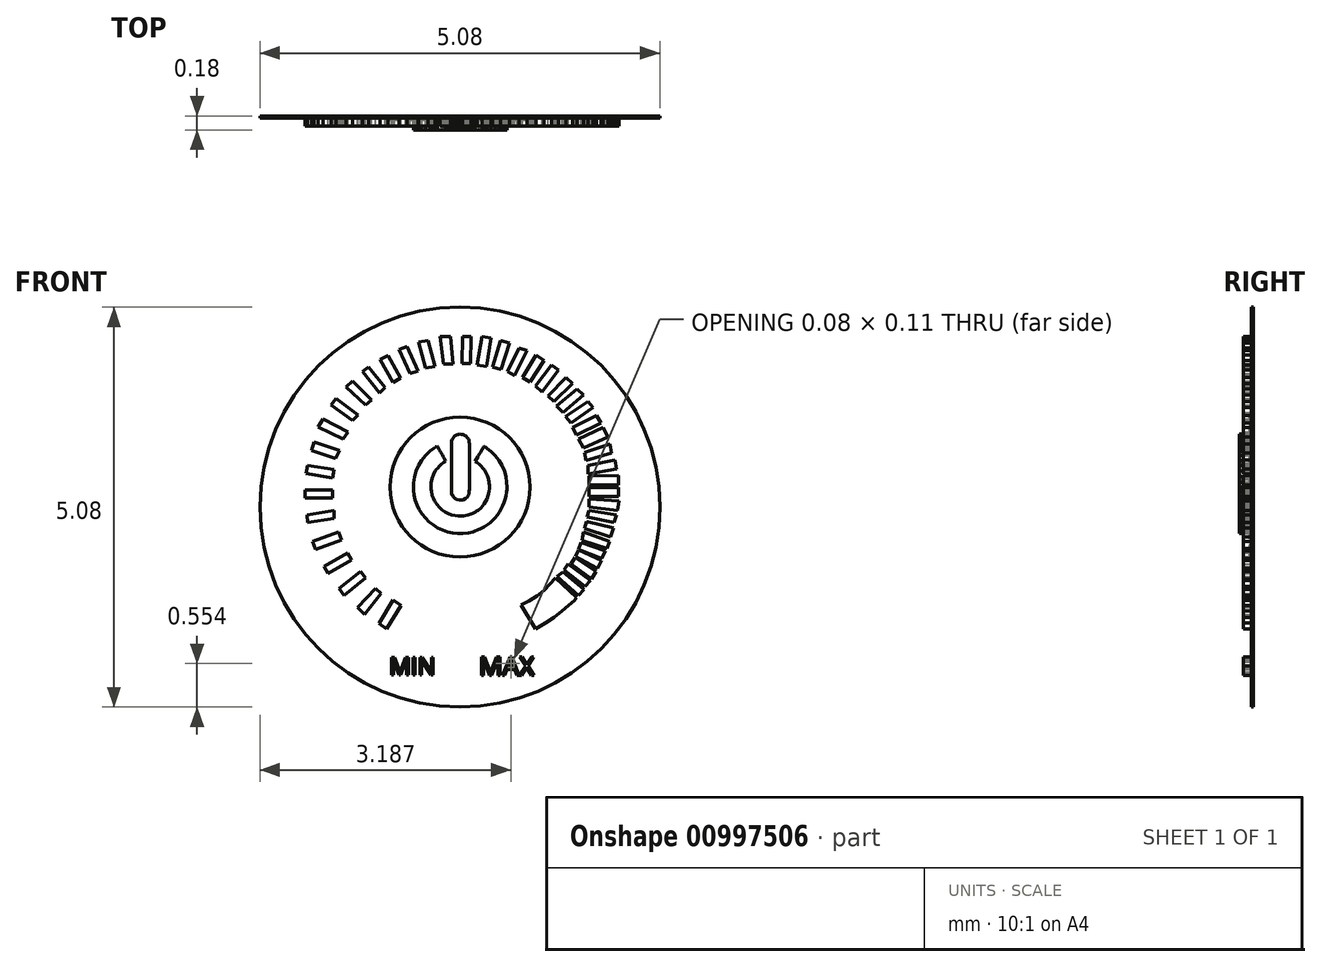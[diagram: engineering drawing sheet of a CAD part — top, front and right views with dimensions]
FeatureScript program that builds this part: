
annotation { "Feature Type Name" : "Feature", "Feature Type Description" : "" }
export const myFeature = defineFeature(function(context is Context, id is Id, definition is map)
    precondition{}
    {
        {
            var Q0;
            Q0=qCreatedBy(makeId("Front.planeOp"),FACE);
            var sketch = newSketch(context, id + "F0", { "sketchPlane" : qUnion([Q0])});
            skCircle(sketch, "E0", {"center": v(0, 0) * mm, "radius": 2.54 * mm});
            skSolve(sketch);
        }
        {
            var Q0;
            Q0 = qSketchRegion(id + "F0", true);
            extrude(context, id + "F1", {"entities" : qUnion([Q0]), "depth" : 0.03 * mm, "offsetDistance" : 25.4 * mm});
        }
        {
            var Q0;
            Q0=qCreatedBy(makeId("Front.planeOp"),FACE);
            var sketch = newSketch(context, id + "F2", { "sketchPlane" : qUnion([Q0])});
            skLineSegment(sketch, "E1", {"start": v(-0.85, -1.18) * mm, "end": v(-1.03, -1.48) * mm});
            skLineSegment(sketch, "E2", {"start": v(-1.03, -1.48) * mm, "end": v(-0.93, -1.55) * mm});
            skLineSegment(sketch, "E3", {"start": v(-0.93, -1.55) * mm, "end": v(-0.75, -1.25) * mm});
            skLineSegment(sketch, "E4", {"start": v(-0.75, -1.25) * mm, "end": v(-0.85, -1.18) * mm});
            skLineSegment(sketch, "E5", {"start": v(-1.3, -1.28) * mm, "end": v(-1.21, -1.36) * mm});
            skLineSegment(sketch, "E6", {"start": v(-1.21, -1.36) * mm, "end": v(-1, -1.1) * mm});
            skLineSegment(sketch, "E7", {"start": v(-1, -1.1) * mm, "end": v(-1.07, -1.03) * mm});
            skLineSegment(sketch, "E8", {"start": v(-1.07, -1.03) * mm, "end": v(-1.3, -1.28) * mm});
            skLineSegment(sketch, "E9", {"start": v(-1.54, -1.03) * mm, "end": v(-1.47, -1.12) * mm});
            skLineSegment(sketch, "E10", {"start": v(-1.47, -1.12) * mm, "end": v(-1.2, -0.9) * mm});
            skLineSegment(sketch, "E11", {"start": v(-1.2, -0.9) * mm, "end": v(-1.27, -0.82) * mm});
            skLineSegment(sketch, "E12", {"start": v(-1.27, -0.82) * mm, "end": v(-1.54, -1.03) * mm});
            skLineSegment(sketch, "E13", {"start": v(-1.73, -0.75) * mm, "end": v(-1.67, -0.85) * mm});
            skLineSegment(sketch, "E14", {"start": v(-1.67, -0.85) * mm, "end": v(-1.38, -0.67) * mm});
            skLineSegment(sketch, "E15", {"start": v(-1.38, -0.67) * mm, "end": v(-1.43, -0.58) * mm});
            skLineSegment(sketch, "E16", {"start": v(-1.43, -0.58) * mm, "end": v(-1.73, -0.75) * mm});
            skLineSegment(sketch, "E17", {"start": v(-1.87, -0.43) * mm, "end": v(-1.83, -0.54) * mm});
            skLineSegment(sketch, "E18", {"start": v(-1.83, -0.54) * mm, "end": v(-1.5, -0.42) * mm});
            skLineSegment(sketch, "E19", {"start": v(-1.5, -0.42) * mm, "end": v(-1.54, -0.32) * mm});
            skLineSegment(sketch, "E20", {"start": v(-1.54, -0.32) * mm, "end": v(-1.87, -0.43) * mm});
            skLineSegment(sketch, "E21", {"start": v(-1.94, -0.1) * mm, "end": v(-1.94, -0.2) * mm});
            skLineSegment(sketch, "E22", {"start": v(-1.94, -0.2) * mm, "end": v(-1.6, -0.14) * mm});
            skLineSegment(sketch, "E23", {"start": v(-1.6, -0.14) * mm, "end": v(-1.6, -0.04) * mm});
            skLineSegment(sketch, "E24", {"start": v(-1.6, -0.04) * mm, "end": v(-1.94, -0.1) * mm});
            skLineSegment(sketch, "E25", {"start": v(-1.97, 0.22) * mm, "end": v(-1.97, 0.12) * mm});
            skLineSegment(sketch, "E26", {"start": v(-1.97, 0.12) * mm, "end": v(-1.62, 0.12) * mm});
            skLineSegment(sketch, "E27", {"start": v(-1.62, 0.12) * mm, "end": v(-1.62, 0.22) * mm});
            skLineSegment(sketch, "E28", {"start": v(-1.62, 0.22) * mm, "end": v(-1.97, 0.22) * mm});
            skLineSegment(sketch, "E29", {"start": v(-1.94, 0.53) * mm, "end": v(-1.96, 0.43) * mm});
            skLineSegment(sketch, "E30", {"start": v(-1.96, 0.43) * mm, "end": v(-1.62, 0.37) * mm});
            skLineSegment(sketch, "E31", {"start": v(-1.62, 0.37) * mm, "end": v(-1.6, 0.48) * mm});
            skLineSegment(sketch, "E32", {"start": v(-1.6, 0.48) * mm, "end": v(-1.94, 0.53) * mm});
            skLineSegment(sketch, "E33", {"start": v(-1.85, 0.82) * mm, "end": v(-1.89, 0.72) * mm});
            skLineSegment(sketch, "E34", {"start": v(-1.89, 0.72) * mm, "end": v(-1.58, 0.62) * mm});
            skLineSegment(sketch, "E35", {"start": v(-1.58, 0.62) * mm, "end": v(-1.53, 0.72) * mm});
            skLineSegment(sketch, "E36", {"start": v(-1.53, 0.72) * mm, "end": v(-1.85, 0.82) * mm});
            skLineSegment(sketch, "E37", {"start": v(-1.74, 1.12) * mm, "end": v(-1.8, 1.02) * mm});
            skLineSegment(sketch, "E38", {"start": v(-1.8, 1.02) * mm, "end": v(-1.48, 0.86) * mm});
            skLineSegment(sketch, "E39", {"start": v(-1.48, 0.86) * mm, "end": v(-1.42, 0.95) * mm});
            skLineSegment(sketch, "E40", {"start": v(-1.42, 0.95) * mm, "end": v(-1.74, 1.12) * mm});
            skLineSegment(sketch, "E41", {"start": v(-1.57, 1.38) * mm, "end": v(-1.64, 1.3) * mm});
            skLineSegment(sketch, "E42", {"start": v(-1.64, 1.3) * mm, "end": v(-1.36, 1.1) * mm});
            skLineSegment(sketch, "E43", {"start": v(-1.36, 1.1) * mm, "end": v(-1.3, 1.17) * mm});
            skLineSegment(sketch, "E44", {"start": v(-1.3, 1.17) * mm, "end": v(-1.57, 1.38) * mm});
            skLineSegment(sketch, "E45", {"start": v(-1.45, 1.53) * mm, "end": v(-1.2, 1.3) * mm});
            skLineSegment(sketch, "E46", {"start": v(-1.2, 1.3) * mm, "end": v(-1.12, 1.36) * mm});
            skLineSegment(sketch, "E47", {"start": v(-1.12, 1.36) * mm, "end": v(-1.36, 1.6) * mm});
            skLineSegment(sketch, "E48", {"start": v(-1.36, 1.6) * mm, "end": v(-1.45, 1.53) * mm});
            skLineSegment(sketch, "E49", {"start": v(-1.24, 1.72) * mm, "end": v(-1.16, 1.78) * mm});
            skLineSegment(sketch, "E50", {"start": v(-1.16, 1.78) * mm, "end": v(-0.95, 1.52) * mm});
            skLineSegment(sketch, "E51", {"start": v(-0.95, 1.52) * mm, "end": v(-1.02, 1.45) * mm});
            skLineSegment(sketch, "E52", {"start": v(-1.02, 1.45) * mm, "end": v(-1.24, 1.72) * mm});
            skLineSegment(sketch, "E53", {"start": v(-1.01, 1.88) * mm, "end": v(-0.85, 1.58) * mm});
            skLineSegment(sketch, "E54", {"start": v(-0.85, 1.58) * mm, "end": v(-0.75, 1.64) * mm});
            skLineSegment(sketch, "E55", {"start": v(-0.75, 1.64) * mm, "end": v(-0.91, 1.93) * mm});
            skLineSegment(sketch, "E56", {"start": v(-0.91, 1.93) * mm, "end": v(-1.01, 1.88) * mm});
            skLineSegment(sketch, "E57", {"start": v(-0.77, 2) * mm, "end": v(-0.63, 1.7) * mm});
            skLineSegment(sketch, "E58", {"start": v(-0.63, 1.7) * mm, "end": v(-0.53, 1.73) * mm});
            skLineSegment(sketch, "E59", {"start": v(-0.53, 1.73) * mm, "end": v(-0.67, 2.04) * mm});
            skLineSegment(sketch, "E60", {"start": v(-0.67, 2.04) * mm, "end": v(-0.77, 2) * mm});
            skLineSegment(sketch, "E61", {"start": v(-0.53, 2.1) * mm, "end": v(-0.4, 2.12) * mm});
            skLineSegment(sketch, "E62", {"start": v(-0.4, 2.12) * mm, "end": v(-0.32, 1.79) * mm});
            skLineSegment(sketch, "E63", {"start": v(-0.32, 1.79) * mm, "end": v(-0.44, 1.77) * mm});
            skLineSegment(sketch, "E64", {"start": v(-0.44, 1.77) * mm, "end": v(-0.53, 2.1) * mm});
            skLineSegment(sketch, "E65", {"start": v(-0.25, 2.17) * mm, "end": v(-0.21, 1.82) * mm});
            skLineSegment(sketch, "E66", {"start": v(-0.21, 1.82) * mm, "end": v(-0.1, 1.82) * mm});
            skLineSegment(sketch, "E67", {"start": v(-0.1, 1.82) * mm, "end": v(-0.12, 2.17) * mm});
            skLineSegment(sketch, "E68", {"start": v(-0.12, 2.17) * mm, "end": v(-0.25, 2.17) * mm});
            skLineSegment(sketch, "E69", {"start": v(0.03, 2.17) * mm, "end": v(0.03, 1.83) * mm});
            skLineSegment(sketch, "E70", {"start": v(0.03, 1.83) * mm, "end": v(0.13, 1.82) * mm});
            skLineSegment(sketch, "E71", {"start": v(0.13, 1.82) * mm, "end": v(0.14, 2.17) * mm});
            skLineSegment(sketch, "E72", {"start": v(0.14, 2.17) * mm, "end": v(0.03, 2.17) * mm});
            skLineSegment(sketch, "E73", {"start": v(0.22, 1.8) * mm, "end": v(0.33, 1.79) * mm});
            skLineSegment(sketch, "E74", {"start": v(0.33, 1.79) * mm, "end": v(0.4, 2.15) * mm});
            skLineSegment(sketch, "E75", {"start": v(0.4, 2.15) * mm, "end": v(0.28, 2.16) * mm});
            skLineSegment(sketch, "E76", {"start": v(0.28, 2.16) * mm, "end": v(0.22, 1.8) * mm});
            skLineSegment(sketch, "E77", {"start": v(0.42, 1.78) * mm, "end": v(0.52, 1.75) * mm});
            skLineSegment(sketch, "E78", {"start": v(0.52, 1.75) * mm, "end": v(0.63, 2.08) * mm});
            skLineSegment(sketch, "E79", {"start": v(0.63, 2.08) * mm, "end": v(0.52, 2.12) * mm});
            skLineSegment(sketch, "E80", {"start": v(0.52, 2.12) * mm, "end": v(0.42, 1.78) * mm});
            skLineSegment(sketch, "E81", {"start": v(0.6, 1.72) * mm, "end": v(0.7, 1.67) * mm});
            skLineSegment(sketch, "E82", {"start": v(0.7, 1.67) * mm, "end": v(0.85, 1.99) * mm});
            skLineSegment(sketch, "E83", {"start": v(0.85, 1.99) * mm, "end": v(0.75, 2.02) * mm});
            skLineSegment(sketch, "E84", {"start": v(0.75, 2.02) * mm, "end": v(0.6, 1.72) * mm});
            skLineSegment(sketch, "E85", {"start": v(0.8, 1.65) * mm, "end": v(0.89, 1.59) * mm});
            skLineSegment(sketch, "E86", {"start": v(0.89, 1.59) * mm, "end": v(1.07, 1.86) * mm});
            skLineSegment(sketch, "E87", {"start": v(1.07, 1.86) * mm, "end": v(0.96, 1.93) * mm});
            skLineSegment(sketch, "E88", {"start": v(0.96, 1.93) * mm, "end": v(0.8, 1.65) * mm});
            skLineSegment(sketch, "E89", {"start": v(0.96, 1.54) * mm, "end": v(1.04, 1.46) * mm});
            skLineSegment(sketch, "E90", {"start": v(1.04, 1.46) * mm, "end": v(1.25, 1.74) * mm});
            skLineSegment(sketch, "E91", {"start": v(1.25, 1.74) * mm, "end": v(1.16, 1.8) * mm});
            skLineSegment(sketch, "E92", {"start": v(1.16, 1.8) * mm, "end": v(0.96, 1.54) * mm});
            skLineSegment(sketch, "E93", {"start": v(1.12, 1.41) * mm, "end": v(1.2, 1.34) * mm});
            skLineSegment(sketch, "E94", {"start": v(1.2, 1.34) * mm, "end": v(1.43, 1.57) * mm});
            skLineSegment(sketch, "E95", {"start": v(1.43, 1.57) * mm, "end": v(1.35, 1.65) * mm});
            skLineSegment(sketch, "E96", {"start": v(1.35, 1.65) * mm, "end": v(1.12, 1.41) * mm});
            skLineSegment(sketch, "E97", {"start": v(1.22, 1.29) * mm, "end": v(1.3, 1.2) * mm});
            skLineSegment(sketch, "E98", {"start": v(1.3, 1.2) * mm, "end": v(1.57, 1.42) * mm});
            skLineSegment(sketch, "E99", {"start": v(1.57, 1.42) * mm, "end": v(1.49, 1.5) * mm});
            skLineSegment(sketch, "E100", {"start": v(1.49, 1.5) * mm, "end": v(1.22, 1.29) * mm});
            skLineSegment(sketch, "E101", {"start": v(1.34, 1.15) * mm, "end": v(1.41, 1.07) * mm});
            skLineSegment(sketch, "E102", {"start": v(1.41, 1.07) * mm, "end": v(1.69, 1.26) * mm});
            skLineSegment(sketch, "E103", {"start": v(1.69, 1.26) * mm, "end": v(1.63, 1.34) * mm});
            skLineSegment(sketch, "E104", {"start": v(1.63, 1.34) * mm, "end": v(1.34, 1.15) * mm});
            skLineSegment(sketch, "E105", {"start": v(1.43, 1) * mm, "end": v(1.48, 0.92) * mm});
            skLineSegment(sketch, "E106", {"start": v(1.48, 0.92) * mm, "end": v(1.8, 1.07) * mm});
            skLineSegment(sketch, "E107", {"start": v(1.8, 1.07) * mm, "end": v(1.74, 1.17) * mm});
            skLineSegment(sketch, "E108", {"start": v(1.74, 1.17) * mm, "end": v(1.43, 1) * mm});
            skLineSegment(sketch, "E109", {"start": v(1.5, 0.86) * mm, "end": v(1.57, 0.75) * mm});
            skLineSegment(sketch, "E110", {"start": v(1.57, 0.75) * mm, "end": v(1.88, 0.9) * mm});
            skLineSegment(sketch, "E111", {"start": v(1.88, 0.9) * mm, "end": v(1.82, 1) * mm});
            skLineSegment(sketch, "E112", {"start": v(1.82, 1) * mm, "end": v(1.5, 0.86) * mm});
            skLineSegment(sketch, "E113", {"start": v(1.58, 0.7) * mm, "end": v(1.6, 0.6) * mm});
            skLineSegment(sketch, "E114", {"start": v(1.6, 0.6) * mm, "end": v(1.93, 0.69) * mm});
            skLineSegment(sketch, "E115", {"start": v(1.93, 0.69) * mm, "end": v(1.9, 0.8) * mm});
            skLineSegment(sketch, "E116", {"start": v(1.9, 0.8) * mm, "end": v(1.58, 0.7) * mm});
            skLineSegment(sketch, "E117", {"start": v(1.62, 0.53) * mm, "end": v(1.62, 0.42) * mm});
            skLineSegment(sketch, "E118", {"start": v(1.62, 0.42) * mm, "end": v(1.99, 0.49) * mm});
            skLineSegment(sketch, "E119", {"start": v(1.99, 0.49) * mm, "end": v(1.97, 0.6) * mm});
            skLineSegment(sketch, "E120", {"start": v(1.97, 0.6) * mm, "end": v(1.62, 0.53) * mm});
            skLineSegment(sketch, "E121", {"start": v(1.64, 0.4) * mm, "end": v(1.64, 0.28) * mm});
            skLineSegment(sketch, "E122", {"start": v(1.64, 0.28) * mm, "end": v(2.02, 0.28) * mm});
            skLineSegment(sketch, "E123", {"start": v(2.02, 0.28) * mm, "end": v(2.02, 0.4) * mm});
            skLineSegment(sketch, "E124", {"start": v(2.02, 0.4) * mm, "end": v(1.64, 0.4) * mm});
            skLineSegment(sketch, "E125", {"start": v(1.64, 0.25) * mm, "end": v(1.64, 0.14) * mm});
            skLineSegment(sketch, "E126", {"start": v(1.64, 0.14) * mm, "end": v(2.02, 0.14) * mm});
            skLineSegment(sketch, "E127", {"start": v(2.02, 0.14) * mm, "end": v(2.02, 0.25) * mm});
            skLineSegment(sketch, "E128", {"start": v(2.02, 0.25) * mm, "end": v(1.64, 0.25) * mm});
            skLineSegment(sketch, "E129", {"start": v(1.64, 0.1) * mm, "end": v(1.64, 0) * mm});
            skLineSegment(sketch, "E130", {"start": v(1.64, 0) * mm, "end": v(2, -0.04) * mm});
            skLineSegment(sketch, "E131", {"start": v(2, -0.04) * mm, "end": v(2.02, 0.08) * mm});
            skLineSegment(sketch, "E132", {"start": v(2.02, 0.08) * mm, "end": v(1.64, 0.1) * mm});
            skLineSegment(sketch, "E133", {"start": v(1.64, -0.04) * mm, "end": v(1.61, -0.12) * mm});
            skLineSegment(sketch, "E134", {"start": v(1.61, -0.12) * mm, "end": v(1.96, -0.2) * mm});
            skLineSegment(sketch, "E135", {"start": v(1.96, -0.2) * mm, "end": v(1.99, -0.1) * mm});
            skLineSegment(sketch, "E136", {"start": v(1.99, -0.1) * mm, "end": v(1.64, -0.04) * mm});
            skLineSegment(sketch, "E137", {"start": v(1.6, -0.19) * mm, "end": v(1.58, -0.27) * mm});
            skLineSegment(sketch, "E138", {"start": v(1.58, -0.27) * mm, "end": v(1.91, -0.38) * mm});
            skLineSegment(sketch, "E139", {"start": v(1.91, -0.38) * mm, "end": v(1.95, -0.27) * mm});
            skLineSegment(sketch, "E140", {"start": v(1.95, -0.27) * mm, "end": v(1.6, -0.19) * mm});
            skLineSegment(sketch, "E141", {"start": v(0.78, -1.24) * mm, "end": v(0.96, -1.55) * mm});
            skLineSegment(sketch, "E142", {"start": v(0.96, -1.55) * mm, "end": v(1.09, -1.47) * mm});
            skLineSegment(sketch, "E143", {"start": v(1.09, -1.47) * mm, "end": v(1.2, -1.4) * mm});
            skLineSegment(sketch, "E144", {"start": v(1.2, -1.4) * mm, "end": v(1.3, -1.32) * mm});
            skLineSegment(sketch, "E145", {"start": v(1.3, -1.32) * mm, "end": v(1.38, -1.25) * mm});
            skLineSegment(sketch, "E146", {"start": v(1.38, -1.25) * mm, "end": v(1.46, -1.19) * mm});
            skLineSegment(sketch, "E147", {"start": v(1.46, -1.19) * mm, "end": v(1.48, -1.15) * mm});
            skLineSegment(sketch, "E148", {"start": v(1.48, -1.15) * mm, "end": v(1.22, -0.9) * mm});
            skLineSegment(sketch, "E149", {"start": v(1.22, -0.9) * mm, "end": v(1.14, -0.98) * mm});
            skLineSegment(sketch, "E150", {"start": v(1.14, -0.98) * mm, "end": v(1.07, -1.06) * mm});
            skLineSegment(sketch, "E151", {"start": v(1.07, -1.06) * mm, "end": v(0.98, -1.13) * mm});
            skLineSegment(sketch, "E152", {"start": v(0.98, -1.13) * mm, "end": v(0.88, -1.2) * mm});
            skLineSegment(sketch, "E153", {"start": v(0.88, -1.2) * mm, "end": v(0.78, -1.24) * mm});
            skLineSegment(sketch, "E154", {"start": v(1.5, -1.12) * mm, "end": v(1.23, -0.88) * mm});
            skLineSegment(sketch, "E155", {"start": v(1.23, -0.88) * mm, "end": v(1.3, -0.82) * mm});
            skLineSegment(sketch, "E156", {"start": v(1.3, -0.82) * mm, "end": v(1.57, -1.05) * mm});
            skLineSegment(sketch, "E157", {"start": v(1.57, -1.05) * mm, "end": v(1.5, -1.12) * mm});
            skLineSegment(sketch, "E158", {"start": v(1.59, -1) * mm, "end": v(1.66, -0.93) * mm});
            skLineSegment(sketch, "E159", {"start": v(1.66, -0.93) * mm, "end": v(1.37, -0.72) * mm});
            skLineSegment(sketch, "E160", {"start": v(1.37, -0.72) * mm, "end": v(1.32, -0.8) * mm});
            skLineSegment(sketch, "E161", {"start": v(1.32, -0.8) * mm, "end": v(1.59, -1) * mm});
            skLineSegment(sketch, "E162", {"start": v(1.57, -0.32) * mm, "end": v(1.55, -0.43) * mm});
            skLineSegment(sketch, "E163", {"start": v(1.55, -0.43) * mm, "end": v(1.87, -0.53) * mm});
            skLineSegment(sketch, "E164", {"start": v(1.87, -0.53) * mm, "end": v(1.9, -0.43) * mm});
            skLineSegment(sketch, "E165", {"start": v(1.9, -0.43) * mm, "end": v(1.57, -0.32) * mm});
            skLineSegment(sketch, "E166", {"start": v(1.8, -0.65) * mm, "end": v(1.85, -0.56) * mm});
            skLineSegment(sketch, "E167", {"start": v(1.85, -0.56) * mm, "end": v(1.54, -0.45) * mm});
            skLineSegment(sketch, "E168", {"start": v(1.54, -0.45) * mm, "end": v(1.5, -0.54) * mm});
            skLineSegment(sketch, "E169", {"start": v(1.5, -0.54) * mm, "end": v(1.8, -0.65) * mm});
            skLineSegment(sketch, "E170", {"start": v(1.5, -0.55) * mm, "end": v(1.47, -0.62) * mm});
            skLineSegment(sketch, "E171", {"start": v(1.47, -0.62) * mm, "end": v(1.75, -0.78) * mm});
            skLineSegment(sketch, "E172", {"start": v(1.75, -0.78) * mm, "end": v(1.8, -0.68) * mm});
            skLineSegment(sketch, "E173", {"start": v(1.8, -0.68) * mm, "end": v(1.5, -0.55) * mm});
            skLineSegment(sketch, "E174", {"start": v(1.67, -0.91) * mm, "end": v(1.73, -0.82) * mm});
            skLineSegment(sketch, "E175", {"start": v(1.73, -0.82) * mm, "end": v(1.46, -0.64) * mm});
            skLineSegment(sketch, "E176", {"start": v(1.46, -0.64) * mm, "end": v(1.41, -0.72) * mm});
            skLineSegment(sketch, "E177", {"start": v(1.41, -0.72) * mm, "end": v(1.67, -0.91) * mm});
            skText(sketch, "E178", { "text": "MIN", "fontName": "OpenSans-Regular.ttf"});
            skText(sketch, "E179", { "text": "MAX", "fontName": "OpenSans-Regular.ttf"});
            const initialGuessF2  = {"E178": [-0.0009, -0.00213, 1, 0, 0.00022], "E179": [0.00024, -0.00214, 1, 0, 0.00024]};
            skSetInitialGuess(sketch, initialGuessF2);
            skSolve(sketch);
        }
        {
            var Q0;
            Q0 = qSketchRegion(id + "F2", true);
            extrude(context, id + "F3", {"entities" : qUnion([Q0]), "depth" : 0.13 * mm, "offsetDistance" : 25.4 * mm});
        }
        {
            var Q0;
            Q0=makeQuery(id+"F1.opExtrude","CAP_FACE",FACE,{"disambiguationData":[OSD([sQuery(id+"F0.wireOp",EDGE,"E0")])],"isStart":false});
            var sketch = newSketch(context, id + "F4", { "sketchPlane" : qUnion([Q0])});
            skCircle(sketch, "E180", {"center": v(0, 0.25) * mm, "radius": 0.89 * mm});
            skSolve(sketch);
        }
        {
            var Q0;
            Q0=makeQuery(id+"F4.imprint","IMPRINT",FACE,{"disambiguationData":[TD([[makeQuery(id+"F4.imprint","IMPRINT",EDGE,{"derivedFrom":sQuery(id+"F4.wireOp",EDGE,"E180")}),1.0]])]});
            extrude(context, id + "F5", {"entities" : qUnion([Q0]), "depth" : 0.03 * mm, "offsetDistance" : 25.4 * mm});
        }
        {
            var Q0;
            Q0=makeQuery(id+"F5.opExtrude","CAP_FACE",FACE,{"disambiguationData":[OSD([sQuery(id+"F4.wireOp",EDGE,"E180")])],"isStart":false});
            var sketch = newSketch(context, id + "F6", { "sketchPlane" : qUnion([Q0])});
            skPoint(sketch, "E181", {"position": v(0, 0.34) * mm});
            skLineSegment(sketch, "E182", {"start": v(-0.02, 0.92) * mm, "end": v(-0.03, 0.92) * mm});
            skLineSegment(sketch, "E183", {"start": v(-0.03, 0.92) * mm, "end": v(-0.05, 0.92) * mm});
            skLineSegment(sketch, "E184", {"start": v(-0.05, 0.92) * mm, "end": v(-0.07, 0.9) * mm});
            skLineSegment(sketch, "E185", {"start": v(-0.07, 0.9) * mm, "end": v(-0.08, 0.88) * mm});
            skLineSegment(sketch, "E186", {"start": v(-0.08, 0.88) * mm, "end": v(-0.1, 0.86) * mm});
            skLineSegment(sketch, "E187", {"start": v(-0.1, 0.86) * mm, "end": v(-0.1, 0.86) * mm});
            skLineSegment(sketch, "E188", {"start": v(-0.1, 0.86) * mm, "end": v(-0.1, 0.84) * mm});
            skLineSegment(sketch, "E189", {"start": v(-0.1, 0.84) * mm, "end": v(-0.1, 0.18) * mm});
            skLineSegment(sketch, "E190", {"start": v(-0.1, 0.18) * mm, "end": v(-0.1, 0.16) * mm});
            skLineSegment(sketch, "E191", {"start": v(-0.1, 0.16) * mm, "end": v(-0.1, 0.15) * mm});
            skLineSegment(sketch, "E192", {"start": v(-0.1, 0.15) * mm, "end": v(-0.09, 0.14) * mm});
            skLineSegment(sketch, "E193", {"start": v(-0.09, 0.14) * mm, "end": v(-0.08, 0.12) * mm});
            skLineSegment(sketch, "E194", {"start": v(-0.08, 0.12) * mm, "end": v(-0.06, 0.11) * mm});
            skLineSegment(sketch, "E195", {"start": v(-0.06, 0.11) * mm, "end": v(-0.05, 0.1) * mm});
            skLineSegment(sketch, "E196", {"start": v(-0.05, 0.1) * mm, "end": v(-0.05, 0.1) * mm});
            skLineSegment(sketch, "E197", {"start": v(-0.05, 0.1) * mm, "end": v(-0.04, 0.1) * mm});
            skLineSegment(sketch, "E198", {"start": v(-0.04, 0.1) * mm, "end": v(0, 0.09) * mm});
            skLineSegment(sketch, "E199", {"start": v(0, 0.09) * mm, "end": v(0.03, 0.09) * mm});
            skLineSegment(sketch, "E200", {"start": v(0.03, 0.09) * mm, "end": v(0.03, 0.1) * mm});
            skLineSegment(sketch, "E201", {"start": v(0.03, 0.1) * mm, "end": v(0.04, 0.1) * mm});
            skLineSegment(sketch, "E202", {"start": v(0.04, 0.1) * mm, "end": v(0.07, 0.1) * mm});
            skLineSegment(sketch, "E203", {"start": v(0.07, 0.1) * mm, "end": v(0.1, 0.13) * mm});
            skLineSegment(sketch, "E204", {"start": v(0.1, 0.13) * mm, "end": v(0.1, 0.14) * mm});
            skLineSegment(sketch, "E205", {"start": v(0.1, 0.14) * mm, "end": v(0.1, 0.14) * mm});
            skLineSegment(sketch, "E206", {"start": v(0.1, 0.14) * mm, "end": v(0.1, 0.15) * mm});
            skLineSegment(sketch, "E207", {"start": v(0.1, 0.15) * mm, "end": v(0.1, 0.15) * mm});
            skLineSegment(sketch, "E208", {"start": v(0.1, 0.15) * mm, "end": v(0.11, 0.16) * mm});
            skLineSegment(sketch, "E209", {"start": v(0.11, 0.16) * mm, "end": v(0.11, 0.17) * mm});
            skLineSegment(sketch, "E210", {"start": v(0.11, 0.17) * mm, "end": v(0.12, 0.18) * mm});
            skLineSegment(sketch, "E211", {"start": v(0.12, 0.18) * mm, "end": v(0.12, 0.19) * mm});
            skLineSegment(sketch, "E212", {"start": v(0.12, 0.19) * mm, "end": v(0.12, 0.2) * mm});
            skLineSegment(sketch, "E213", {"start": v(0.12, 0.2) * mm, "end": v(0.12, 0.22) * mm});
            skLineSegment(sketch, "E214", {"start": v(0.12, 0.22) * mm, "end": v(0.12, 0.24) * mm});
            skLineSegment(sketch, "E215", {"start": v(0.12, 0.24) * mm, "end": v(0.12, 0.27) * mm});
            skLineSegment(sketch, "E216", {"start": v(0.12, 0.27) * mm, "end": v(0.12, 0.3) * mm});
            skLineSegment(sketch, "E217", {"start": v(0.12, 0.3) * mm, "end": v(0.12, 0.35) * mm});
            skLineSegment(sketch, "E218", {"start": v(0.12, 0.35) * mm, "end": v(0.12, 0.4) * mm});
            skLineSegment(sketch, "E219", {"start": v(0.12, 0.4) * mm, "end": v(0.12, 0.45) * mm});
            skLineSegment(sketch, "E220", {"start": v(0.12, 0.45) * mm, "end": v(0.12, 0.5) * mm});
            skLineSegment(sketch, "E221", {"start": v(0.12, 0.5) * mm, "end": v(0.12, 0.5) * mm});
            skLineSegment(sketch, "E222", {"start": v(0.12, 0.5) * mm, "end": v(0.12, 0.53) * mm});
            skLineSegment(sketch, "E223", {"start": v(0.12, 0.53) * mm, "end": v(0.12, 0.6) * mm});
            skLineSegment(sketch, "E224", {"start": v(0.12, 0.6) * mm, "end": v(0.12, 0.68) * mm});
            skLineSegment(sketch, "E225", {"start": v(0.12, 0.68) * mm, "end": v(0.12, 0.73) * mm});
            skLineSegment(sketch, "E226", {"start": v(0.12, 0.73) * mm, "end": v(0.12, 0.77) * mm});
            skLineSegment(sketch, "E227", {"start": v(0.12, 0.77) * mm, "end": v(0.12, 0.8) * mm});
            skLineSegment(sketch, "E228", {"start": v(0.12, 0.8) * mm, "end": v(0.12, 0.82) * mm});
            skLineSegment(sketch, "E229", {"start": v(0.12, 0.82) * mm, "end": v(0.12, 0.84) * mm});
            skLineSegment(sketch, "E230", {"start": v(0.12, 0.84) * mm, "end": v(0.12, 0.84) * mm});
            skLineSegment(sketch, "E231", {"start": v(0.12, 0.84) * mm, "end": v(0.11, 0.84) * mm});
            skLineSegment(sketch, "E232", {"start": v(0.11, 0.84) * mm, "end": v(0.11, 0.85) * mm});
            skLineSegment(sketch, "E233", {"start": v(0.11, 0.85) * mm, "end": v(0.1, 0.87) * mm});
            skLineSegment(sketch, "E234", {"start": v(0.1, 0.87) * mm, "end": v(0.1, 0.89) * mm});
            skLineSegment(sketch, "E235", {"start": v(0.1, 0.89) * mm, "end": v(0.08, 0.9) * mm});
            skLineSegment(sketch, "E236", {"start": v(0.08, 0.9) * mm, "end": v(0.06, 0.91) * mm});
            skLineSegment(sketch, "E237", {"start": v(0.06, 0.91) * mm, "end": v(0.06, 0.92) * mm});
            skLineSegment(sketch, "E238", {"start": v(0.06, 0.92) * mm, "end": v(0.05, 0.92) * mm});
            skLineSegment(sketch, "E239", {"start": v(0.05, 0.92) * mm, "end": v(0.04, 0.92) * mm});
            skLineSegment(sketch, "E240", {"start": v(0.04, 0.92) * mm, "end": v(0.02, 0.93) * mm});
            skLineSegment(sketch, "E241", {"start": v(0.02, 0.93) * mm, "end": v(0, 0.93) * mm});
            skLineSegment(sketch, "E242", {"start": v(0, 0.93) * mm, "end": v(-0.02, 0.93) * mm});
            skLineSegment(sketch, "E243", {"start": v(-0.02, 0.93) * mm, "end": v(-0.02, 0.92) * mm});
            skLineSegment(sketch, "E244", {"start": v(-0.32, 0.76) * mm, "end": v(-0.33, 0.75) * mm});
            skLineSegment(sketch, "E245", {"start": v(-0.33, 0.75) * mm, "end": v(-0.38, 0.7) * mm});
            skLineSegment(sketch, "E246", {"start": v(-0.38, 0.7) * mm, "end": v(-0.44, 0.65) * mm});
            skLineSegment(sketch, "E247", {"start": v(-0.44, 0.65) * mm, "end": v(-0.49, 0.6) * mm});
            skLineSegment(sketch, "E248", {"start": v(-0.49, 0.6) * mm, "end": v(-0.53, 0.53) * mm});
            skLineSegment(sketch, "E249", {"start": v(-0.53, 0.53) * mm, "end": v(-0.56, 0.46) * mm});
            skLineSegment(sketch, "E250", {"start": v(-0.56, 0.46) * mm, "end": v(-0.58, 0.38) * mm});
            skLineSegment(sketch, "E251", {"start": v(-0.58, 0.38) * mm, "end": v(-0.59, 0.3) * mm});
            skLineSegment(sketch, "E252", {"start": v(-0.59, 0.3) * mm, "end": v(-0.6, 0.25) * mm});
            skLineSegment(sketch, "E253", {"start": v(-0.6, 0.25) * mm, "end": v(-0.6, 0.23) * mm});
            skLineSegment(sketch, "E254", {"start": v(-0.6, 0.23) * mm, "end": v(-0.59, 0.21) * mm});
            skLineSegment(sketch, "E255", {"start": v(-0.59, 0.21) * mm, "end": v(-0.58, 0.16) * mm});
            skLineSegment(sketch, "E256", {"start": v(-0.58, 0.16) * mm, "end": v(-0.57, 0.09) * mm});
            skLineSegment(sketch, "E257", {"start": v(-0.57, 0.09) * mm, "end": v(-0.54, 0.02) * mm});
            skLineSegment(sketch, "E258", {"start": v(-0.54, 0.02) * mm, "end": v(-0.51, -0.04) * mm});
            skLineSegment(sketch, "E259", {"start": v(-0.51, -0.04) * mm, "end": v(-0.48, -0.1) * mm});
            skLineSegment(sketch, "E260", {"start": v(-0.48, -0.1) * mm, "end": v(-0.44, -0.15) * mm});
            skLineSegment(sketch, "E261", {"start": v(-0.44, -0.15) * mm, "end": v(-0.39, -0.2) * mm});
            skLineSegment(sketch, "E262", {"start": v(-0.39, -0.2) * mm, "end": v(-0.34, -0.24) * mm});
            skLineSegment(sketch, "E263", {"start": v(-0.34, -0.24) * mm, "end": v(-0.28, -0.27) * mm});
            skLineSegment(sketch, "E264", {"start": v(-0.28, -0.27) * mm, "end": v(-0.22, -0.3) * mm});
            skLineSegment(sketch, "E265", {"start": v(-0.22, -0.3) * mm, "end": v(-0.16, -0.32) * mm});
            skLineSegment(sketch, "E266", {"start": v(-0.16, -0.32) * mm, "end": v(-0.1, -0.34) * mm});
            skLineSegment(sketch, "E267", {"start": v(-0.1, -0.34) * mm, "end": v(-0.02, -0.34) * mm});
            skLineSegment(sketch, "E268", {"start": v(-0.02, -0.34) * mm, "end": v(0.05, -0.34) * mm});
            skLineSegment(sketch, "E269", {"start": v(0.05, -0.34) * mm, "end": v(0.12, -0.33) * mm});
            skLineSegment(sketch, "E270", {"start": v(0.12, -0.33) * mm, "end": v(0.17, -0.32) * mm});
            skLineSegment(sketch, "E271", {"start": v(0.17, -0.32) * mm, "end": v(0.19, -0.32) * mm});
            skLineSegment(sketch, "E272", {"start": v(0.19, -0.32) * mm, "end": v(0.2, -0.31) * mm});
            skLineSegment(sketch, "E273", {"start": v(0.2, -0.31) * mm, "end": v(0.23, -0.3) * mm});
            skLineSegment(sketch, "E274", {"start": v(0.23, -0.3) * mm, "end": v(0.27, -0.28) * mm});
            skLineSegment(sketch, "E275", {"start": v(0.27, -0.28) * mm, "end": v(0.31, -0.26) * mm});
            skLineSegment(sketch, "E276", {"start": v(0.31, -0.26) * mm, "end": v(0.35, -0.23) * mm});
            skLineSegment(sketch, "E277", {"start": v(0.35, -0.23) * mm, "end": v(0.39, -0.2) * mm});
            skLineSegment(sketch, "E278", {"start": v(0.39, -0.2) * mm, "end": v(0.42, -0.18) * mm});
            skLineSegment(sketch, "E279", {"start": v(0.42, -0.18) * mm, "end": v(0.45, -0.14) * mm});
            skLineSegment(sketch, "E280", {"start": v(0.45, -0.14) * mm, "end": v(0.48, -0.1) * mm});
            skLineSegment(sketch, "E281", {"start": v(0.48, -0.1) * mm, "end": v(0.5, -0.07) * mm});
            skLineSegment(sketch, "E282", {"start": v(0.5, -0.07) * mm, "end": v(0.53, -0.03) * mm});
            skLineSegment(sketch, "E283", {"start": v(0.53, -0.03) * mm, "end": v(0.55, 0) * mm});
            skLineSegment(sketch, "E284", {"start": v(0.55, 0) * mm, "end": v(0.57, 0.05) * mm});
            skLineSegment(sketch, "E285", {"start": v(0.57, 0.05) * mm, "end": v(0.58, 0.1) * mm});
            skLineSegment(sketch, "E286", {"start": v(0.58, 0.1) * mm, "end": v(0.6, 0.14) * mm});
            skLineSegment(sketch, "E287", {"start": v(0.6, 0.14) * mm, "end": v(0.6, 0.18) * mm});
            skLineSegment(sketch, "E288", {"start": v(0.6, 0.18) * mm, "end": v(0.6, 0.22) * mm});
            skLineSegment(sketch, "E289", {"start": v(0.6, 0.22) * mm, "end": v(0.6, 0.23) * mm});
            skLineSegment(sketch, "E290", {"start": v(0.6, 0.23) * mm, "end": v(0.6, 0.25) * mm});
            skLineSegment(sketch, "E291", {"start": v(0.6, 0.25) * mm, "end": v(0.6, 0.3) * mm});
            skLineSegment(sketch, "E292", {"start": v(0.6, 0.3) * mm, "end": v(0.59, 0.38) * mm});
            skLineSegment(sketch, "E293", {"start": v(0.59, 0.38) * mm, "end": v(0.57, 0.46) * mm});
            skLineSegment(sketch, "E294", {"start": v(0.57, 0.46) * mm, "end": v(0.54, 0.53) * mm});
            skLineSegment(sketch, "E295", {"start": v(0.54, 0.53) * mm, "end": v(0.5, 0.6) * mm});
            skLineSegment(sketch, "E296", {"start": v(0.5, 0.6) * mm, "end": v(0.45, 0.65) * mm});
            skLineSegment(sketch, "E297", {"start": v(0.45, 0.65) * mm, "end": v(0.4, 0.7) * mm});
            skLineSegment(sketch, "E298", {"start": v(0.4, 0.7) * mm, "end": v(0.35, 0.74) * mm});
            skLineSegment(sketch, "E299", {"start": v(0.35, 0.74) * mm, "end": v(0.33, 0.76) * mm});
            skLineSegment(sketch, "E300", {"start": v(0.33, 0.76) * mm, "end": v(0.33, 0.76) * mm});
            skLineSegment(sketch, "E301", {"start": v(0.33, 0.76) * mm, "end": v(0.32, 0.76) * mm});
            skLineSegment(sketch, "E302", {"start": v(0.32, 0.76) * mm, "end": v(0.32, 0.77) * mm});
            skLineSegment(sketch, "E303", {"start": v(0.32, 0.77) * mm, "end": v(0.3, 0.77) * mm});
            skLineSegment(sketch, "E304", {"start": v(0.3, 0.77) * mm, "end": v(0.3, 0.77) * mm});
            skLineSegment(sketch, "E305", {"start": v(0.3, 0.77) * mm, "end": v(0.3, 0.76) * mm});
            skLineSegment(sketch, "E306", {"start": v(0.3, 0.76) * mm, "end": v(0.3, 0.75) * mm});
            skLineSegment(sketch, "E307", {"start": v(0.3, 0.75) * mm, "end": v(0.28, 0.74) * mm});
            skLineSegment(sketch, "E308", {"start": v(0.28, 0.74) * mm, "end": v(0.28, 0.74) * mm});
            skLineSegment(sketch, "E309", {"start": v(0.28, 0.74) * mm, "end": v(0.28, 0.73) * mm});
            skLineSegment(sketch, "E310", {"start": v(0.28, 0.73) * mm, "end": v(0.27, 0.72) * mm});
            skLineSegment(sketch, "E311", {"start": v(0.27, 0.72) * mm, "end": v(0.26, 0.7) * mm});
            skLineSegment(sketch, "E312", {"start": v(0.26, 0.7) * mm, "end": v(0.24, 0.67) * mm});
            skLineSegment(sketch, "E313", {"start": v(0.24, 0.67) * mm, "end": v(0.23, 0.65) * mm});
            skLineSegment(sketch, "E314", {"start": v(0.23, 0.65) * mm, "end": v(0.23, 0.64) * mm});
            skLineSegment(sketch, "E315", {"start": v(0.23, 0.64) * mm, "end": v(0.2, 0.58) * mm});
            skLineSegment(sketch, "E316", {"start": v(0.2, 0.58) * mm, "end": v(0.22, 0.56) * mm});
            skLineSegment(sketch, "E317", {"start": v(0.22, 0.56) * mm, "end": v(0.22, 0.55) * mm});
            skLineSegment(sketch, "E318", {"start": v(0.22, 0.55) * mm, "end": v(0.24, 0.54) * mm});
            skLineSegment(sketch, "E319", {"start": v(0.24, 0.54) * mm, "end": v(0.27, 0.51) * mm});
            skLineSegment(sketch, "E320", {"start": v(0.27, 0.51) * mm, "end": v(0.3, 0.49) * mm});
            skLineSegment(sketch, "E321", {"start": v(0.3, 0.49) * mm, "end": v(0.3, 0.47) * mm});
            skLineSegment(sketch, "E322", {"start": v(0.3, 0.47) * mm, "end": v(0.31, 0.46) * mm});
            skLineSegment(sketch, "E323", {"start": v(0.31, 0.46) * mm, "end": v(0.32, 0.45) * mm});
            skLineSegment(sketch, "E324", {"start": v(0.32, 0.45) * mm, "end": v(0.33, 0.43) * mm});
            skLineSegment(sketch, "E325", {"start": v(0.33, 0.43) * mm, "end": v(0.35, 0.39) * mm});
            skLineSegment(sketch, "E326", {"start": v(0.35, 0.39) * mm, "end": v(0.36, 0.35) * mm});
            skLineSegment(sketch, "E327", {"start": v(0.36, 0.35) * mm, "end": v(0.37, 0.32) * mm});
            skLineSegment(sketch, "E328", {"start": v(0.37, 0.32) * mm, "end": v(0.37, 0.31) * mm});
            skLineSegment(sketch, "E329", {"start": v(0.37, 0.31) * mm, "end": v(0.37, 0.3) * mm});
            skLineSegment(sketch, "E330", {"start": v(0.37, 0.3) * mm, "end": v(0.37, 0.28) * mm});
            skLineSegment(sketch, "E331", {"start": v(0.37, 0.28) * mm, "end": v(0.37, 0.24) * mm});
            skLineSegment(sketch, "E332", {"start": v(0.37, 0.24) * mm, "end": v(0.37, 0.2) * mm});
            skLineSegment(sketch, "E333", {"start": v(0.37, 0.2) * mm, "end": v(0.37, 0.17) * mm});
            skLineSegment(sketch, "E334", {"start": v(0.37, 0.17) * mm, "end": v(0.36, 0.16) * mm});
            skLineSegment(sketch, "E335", {"start": v(0.36, 0.16) * mm, "end": v(0.36, 0.15) * mm});
            skLineSegment(sketch, "E336", {"start": v(0.36, 0.15) * mm, "end": v(0.34, 0.1) * mm});
            skLineSegment(sketch, "E337", {"start": v(0.34, 0.1) * mm, "end": v(0.3, 0.04) * mm});
            skLineSegment(sketch, "E338", {"start": v(0.3, 0.04) * mm, "end": v(0.26, 0) * mm});
            skLineSegment(sketch, "E339", {"start": v(0.26, 0) * mm, "end": v(0.23, -0.04) * mm});
            skLineSegment(sketch, "E340", {"start": v(0.23, -0.04) * mm, "end": v(0.21, -0.05) * mm});
            skLineSegment(sketch, "E341", {"start": v(0.21, -0.05) * mm, "end": v(0.2, -0.06) * mm});
            skLineSegment(sketch, "E342", {"start": v(0.2, -0.06) * mm, "end": v(0.16, -0.08) * mm});
            skLineSegment(sketch, "E343", {"start": v(0.16, -0.08) * mm, "end": v(0.1, -0.1) * mm});
            skLineSegment(sketch, "E344", {"start": v(0.1, -0.1) * mm, "end": v(0.05, -0.11) * mm});
            skLineSegment(sketch, "E345", {"start": v(0.05, -0.11) * mm, "end": v(0, -0.11) * mm});
            skLineSegment(sketch, "E346", {"start": v(0, -0.11) * mm, "end": v(-0.01, -0.11) * mm});
            skLineSegment(sketch, "E347", {"start": v(-0.01, -0.11) * mm, "end": v(-0.02, -0.11) * mm});
            skLineSegment(sketch, "E348", {"start": v(-0.02, -0.11) * mm, "end": v(-0.06, -0.1) * mm});
            skLineSegment(sketch, "E349", {"start": v(-0.06, -0.1) * mm, "end": v(-0.1, -0.1) * mm});
            skLineSegment(sketch, "E350", {"start": v(-0.1, -0.1) * mm, "end": v(-0.15, -0.08) * mm});
            skLineSegment(sketch, "E351", {"start": v(-0.15, -0.08) * mm, "end": v(-0.19, -0.06) * mm});
            skLineSegment(sketch, "E352", {"start": v(-0.19, -0.06) * mm, "end": v(-0.22, -0.04) * mm});
            skLineSegment(sketch, "E353", {"start": v(-0.22, -0.04) * mm, "end": v(-0.26, 0) * mm});
            skLineSegment(sketch, "E354", {"start": v(-0.26, 0) * mm, "end": v(-0.29, 0.03) * mm});
            skLineSegment(sketch, "E355", {"start": v(-0.29, 0.03) * mm, "end": v(-0.3, 0.06) * mm});
            skLineSegment(sketch, "E356", {"start": v(-0.3, 0.06) * mm, "end": v(-0.31, 0.07) * mm});
            skLineSegment(sketch, "E357", {"start": v(-0.31, 0.07) * mm, "end": v(-0.32, 0.08) * mm});
            skLineSegment(sketch, "E358", {"start": v(-0.32, 0.08) * mm, "end": v(-0.33, 0.1) * mm});
            skLineSegment(sketch, "E359", {"start": v(-0.33, 0.1) * mm, "end": v(-0.35, 0.15) * mm});
            skLineSegment(sketch, "E360", {"start": v(-0.35, 0.15) * mm, "end": v(-0.36, 0.2) * mm});
            skLineSegment(sketch, "E361", {"start": v(-0.36, 0.2) * mm, "end": v(-0.36, 0.23) * mm});
            skLineSegment(sketch, "E362", {"start": v(-0.36, 0.23) * mm, "end": v(-0.36, 0.24) * mm});
            skLineSegment(sketch, "E363", {"start": v(-0.36, 0.24) * mm, "end": v(-0.36, 0.25) * mm});
            skLineSegment(sketch, "E364", {"start": v(-0.36, 0.25) * mm, "end": v(-0.36, 0.3) * mm});
            skLineSegment(sketch, "E365", {"start": v(-0.36, 0.3) * mm, "end": v(-0.35, 0.36) * mm});
            skLineSegment(sketch, "E366", {"start": v(-0.35, 0.36) * mm, "end": v(-0.33, 0.4) * mm});
            skLineSegment(sketch, "E367", {"start": v(-0.33, 0.4) * mm, "end": v(-0.3, 0.45) * mm});
            skLineSegment(sketch, "E368", {"start": v(-0.3, 0.45) * mm, "end": v(-0.3, 0.46) * mm});
            skLineSegment(sketch, "E369", {"start": v(-0.3, 0.46) * mm, "end": v(-0.3, 0.47) * mm});
            skLineSegment(sketch, "E370", {"start": v(-0.3, 0.47) * mm, "end": v(-0.28, 0.49) * mm});
            skLineSegment(sketch, "E371", {"start": v(-0.28, 0.49) * mm, "end": v(-0.26, 0.51) * mm});
            skLineSegment(sketch, "E372", {"start": v(-0.26, 0.51) * mm, "end": v(-0.23, 0.54) * mm});
            skLineSegment(sketch, "E373", {"start": v(-0.23, 0.54) * mm, "end": v(-0.2, 0.55) * mm});
            skLineSegment(sketch, "E374", {"start": v(-0.2, 0.55) * mm, "end": v(-0.2, 0.56) * mm});
            skLineSegment(sketch, "E375", {"start": v(-0.2, 0.56) * mm, "end": v(-0.2, 0.56) * mm});
            skLineSegment(sketch, "E376", {"start": v(-0.2, 0.56) * mm, "end": v(-0.2, 0.57) * mm});
            skLineSegment(sketch, "E377", {"start": v(-0.2, 0.57) * mm, "end": v(-0.18, 0.57) * mm});
            skLineSegment(sketch, "E378", {"start": v(-0.18, 0.57) * mm, "end": v(-0.18, 0.58) * mm});
            skLineSegment(sketch, "E379", {"start": v(-0.18, 0.58) * mm, "end": v(-0.18, 0.58) * mm});
            skLineSegment(sketch, "E380", {"start": v(-0.18, 0.5) * mm, "end": v(-0.18, 0.5) * mm});
            skLineSegment(sketch, "E381", {"start": v(-0.18, 0.58) * mm, "end": v(-0.18, 0.59) * mm});
            skLineSegment(sketch, "E382", {"start": v(-0.18, 0.59) * mm, "end": v(-0.18, 0.6) * mm});
            skLineSegment(sketch, "E383", {"start": v(-0.18, 0.6) * mm, "end": v(-0.2, 0.61) * mm});
            skLineSegment(sketch, "E384", {"start": v(-0.2, 0.61) * mm, "end": v(-0.2, 0.63) * mm});
            skLineSegment(sketch, "E385", {"start": v(-0.2, 0.63) * mm, "end": v(-0.2, 0.64) * mm});
            skLineSegment(sketch, "E386", {"start": v(-0.2, 0.64) * mm, "end": v(-0.22, 0.66) * mm});
            skLineSegment(sketch, "E387", {"start": v(-0.22, 0.66) * mm, "end": v(-0.23, 0.68) * mm});
            skLineSegment(sketch, "E388", {"start": v(-0.23, 0.68) * mm, "end": v(-0.24, 0.7) * mm});
            skLineSegment(sketch, "E389", {"start": v(-0.24, 0.7) * mm, "end": v(-0.25, 0.72) * mm});
            skLineSegment(sketch, "E390", {"start": v(-0.25, 0.72) * mm, "end": v(-0.26, 0.73) * mm});
            skLineSegment(sketch, "E391", {"start": v(-0.26, 0.73) * mm, "end": v(-0.27, 0.75) * mm});
            skLineSegment(sketch, "E392", {"start": v(-0.27, 0.75) * mm, "end": v(-0.28, 0.76) * mm});
            skLineSegment(sketch, "E393", {"start": v(-0.28, 0.76) * mm, "end": v(-0.28, 0.77) * mm});
            skLineSegment(sketch, "E394", {"start": v(-0.28, 0.77) * mm, "end": v(-0.28, 0.78) * mm});
            skLineSegment(sketch, "E395", {"start": v(-0.28, 0.78) * mm, "end": v(-0.29, 0.78) * mm});
            skLineSegment(sketch, "E396", {"start": v(-0.29, 0.78) * mm, "end": v(-0.29, 0.78) * mm});
            skLineSegment(sketch, "E397", {"start": v(-0.29, 0.78) * mm, "end": v(-0.3, 0.77) * mm});
            skLineSegment(sketch, "E398", {"start": v(-0.3, 0.77) * mm, "end": v(-0.3, 0.77) * mm});
            skLineSegment(sketch, "E399", {"start": v(-0.3, 0.77) * mm, "end": v(-0.31, 0.76) * mm});
            skLineSegment(sketch, "E400", {"start": v(-0.31, 0.76) * mm, "end": v(-0.32, 0.76) * mm});
            skLineSegment(sketch, "E401", {"start": v(-0.3, 0.77) * mm, "end": v(-0.29, 0.78) * mm});
            skLineSegment(sketch, "E402", {"start": v(-0.32, 0.76) * mm, "end": v(-0.34, 0.75) * mm});
            skLineSegment(sketch, "E403", {"start": v(-0.34, 0.75) * mm, "end": v(-0.39, 0.71) * mm});
            skLineSegment(sketch, "E404", {"start": v(-0.39, 0.71) * mm, "end": v(-0.44, 0.66) * mm});
            skLineSegment(sketch, "E405", {"start": v(-0.44, 0.66) * mm, "end": v(-0.5, 0.6) * mm});
            skLineSegment(sketch, "E406", {"start": v(-0.5, 0.6) * mm, "end": v(-0.53, 0.53) * mm});
            skLineSegment(sketch, "E407", {"start": v(-0.56, 0.46) * mm, "end": v(-0.58, 0.39) * mm});
            skLineSegment(sketch, "E408", {"start": v(-0.58, 0.39) * mm, "end": v(-0.6, 0.3) * mm});
            skLineSegment(sketch, "E409", {"start": v(-0.6, 0.3) * mm, "end": v(-0.6, 0.25) * mm});
            skLineSegment(sketch, "E410", {"start": v(-0.6, 0.23) * mm, "end": v(-0.6, 0.21) * mm});
            skLineSegment(sketch, "E411", {"start": v(-0.6, 0.21) * mm, "end": v(-0.59, 0.16) * mm});
            skLineSegment(sketch, "E412", {"start": v(-0.59, 0.16) * mm, "end": v(-0.57, 0.09) * mm});
            skLineSegment(sketch, "E413", {"start": v(-0.57, 0.09) * mm, "end": v(-0.55, 0.02) * mm});
            skLineSegment(sketch, "E414", {"start": v(-0.55, 0.02) * mm, "end": v(-0.52, -0.04) * mm});
            skLineSegment(sketch, "E415", {"start": v(-0.52, -0.04) * mm, "end": v(-0.48, -0.1) * mm});
            skLineSegment(sketch, "E416", {"start": v(-0.44, -0.15) * mm, "end": v(-0.4, -0.2) * mm});
            skLineSegment(sketch, "E417", {"start": v(-0.4, -0.2) * mm, "end": v(-0.34, -0.23) * mm});
            skLineSegment(sketch, "E418", {"start": v(-0.34, -0.23) * mm, "end": v(-0.28, -0.27) * mm});
            skLineSegment(sketch, "E419", {"start": v(-0.1, -0.34) * mm, "end": v(-0.03, -0.34) * mm});
            skLineSegment(sketch, "E420", {"start": v(-0.03, -0.34) * mm, "end": v(0.04, -0.34) * mm});
            skLineSegment(sketch, "E421", {"start": v(0.04, -0.34) * mm, "end": v(0.11, -0.33) * mm});
            skLineSegment(sketch, "E422", {"start": v(0.11, -0.33) * mm, "end": v(0.17, -0.32) * mm});
            skLineSegment(sketch, "E423", {"start": v(0.17, -0.32) * mm, "end": v(0.18, -0.31) * mm});
            skLineSegment(sketch, "E424", {"start": v(0.18, -0.31) * mm, "end": v(0.2, -0.31) * mm});
            skLineSegment(sketch, "E425", {"start": v(0.27, -0.28) * mm, "end": v(0.3, -0.26) * mm});
            skLineSegment(sketch, "E426", {"start": v(0.3, -0.26) * mm, "end": v(0.35, -0.23) * mm});
            skLineSegment(sketch, "E427", {"start": v(0.35, -0.23) * mm, "end": v(0.38, -0.2) * mm});
            skLineSegment(sketch, "E428", {"start": v(0.38, -0.2) * mm, "end": v(0.42, -0.18) * mm});
            skLineSegment(sketch, "E429", {"start": v(0.55, 0) * mm, "end": v(0.56, 0.05) * mm});
            skLineSegment(sketch, "E430", {"start": v(0.56, 0.05) * mm, "end": v(0.58, 0.1) * mm});
            skLineSegment(sketch, "E431", {"start": v(0.58, 0.1) * mm, "end": v(0.59, 0.14) * mm});
            skLineSegment(sketch, "E432", {"start": v(0.59, 0.14) * mm, "end": v(0.6, 0.18) * mm});
            skLineSegment(sketch, "E433", {"start": v(0.6, 0.3) * mm, "end": v(0.58, 0.38) * mm});
            skLineSegment(sketch, "E434", {"start": v(0.58, 0.38) * mm, "end": v(0.56, 0.46) * mm});
            skLineSegment(sketch, "E435", {"start": v(0.56, 0.46) * mm, "end": v(0.53, 0.53) * mm});
            skLineSegment(sketch, "E436", {"start": v(0.53, 0.53) * mm, "end": v(0.5, 0.6) * mm});
            skLineSegment(sketch, "E437", {"start": v(0.4, 0.7) * mm, "end": v(0.35, 0.75) * mm});
            skLineSegment(sketch, "E438", {"start": v(0.35, 0.75) * mm, "end": v(0.33, 0.76) * mm});
            skLineSegment(sketch, "E439", {"start": v(0.32, 0.76) * mm, "end": v(0.31, 0.77) * mm});
            skLineSegment(sketch, "E440", {"start": v(0.31, 0.77) * mm, "end": v(0.3, 0.77) * mm});
            skLineSegment(sketch, "E441", {"start": v(0.3, 0.76) * mm, "end": v(0.29, 0.75) * mm});
            skLineSegment(sketch, "E442", {"start": v(0.29, 0.75) * mm, "end": v(0.28, 0.74) * mm});
            skLineSegment(sketch, "E443", {"start": v(0.27, 0.72) * mm, "end": v(0.25, 0.7) * mm});
            skLineSegment(sketch, "E444", {"start": v(0.25, 0.7) * mm, "end": v(0.24, 0.67) * mm});
            skLineSegment(sketch, "E445", {"start": v(0.23, 0.65) * mm, "end": v(0.22, 0.64) * mm});
            skLineSegment(sketch, "E446", {"start": v(0.22, 0.64) * mm, "end": v(0.19, 0.58) * mm});
            skLineSegment(sketch, "E447", {"start": v(0.19, 0.58) * mm, "end": v(0.21, 0.56) * mm});
            skLineSegment(sketch, "E448", {"start": v(0.21, 0.56) * mm, "end": v(0.22, 0.55) * mm});
            skLineSegment(sketch, "E449", {"start": v(0.24, 0.54) * mm, "end": v(0.26, 0.51) * mm});
            skLineSegment(sketch, "E450", {"start": v(0.26, 0.51) * mm, "end": v(0.29, 0.49) * mm});
            skLineSegment(sketch, "E451", {"start": v(0.29, 0.49) * mm, "end": v(0.3, 0.47) * mm});
            skLineSegment(sketch, "E452", {"start": v(0.3, 0.47) * mm, "end": v(0.3, 0.46) * mm});
            skLineSegment(sketch, "E453", {"start": v(0.3, 0.46) * mm, "end": v(0.31, 0.45) * mm});
            skLineSegment(sketch, "E454", {"start": v(0.31, 0.45) * mm, "end": v(0.33, 0.43) * mm});
            skLineSegment(sketch, "E455", {"start": v(0.33, 0.43) * mm, "end": v(0.35, 0.4) * mm});
            skLineSegment(sketch, "E456", {"start": v(0.35, 0.4) * mm, "end": v(0.36, 0.35) * mm});
            skLineSegment(sketch, "E457", {"start": v(0.36, 0.35) * mm, "end": v(0.36, 0.32) * mm});
            skLineSegment(sketch, "E458", {"start": v(0.36, 0.32) * mm, "end": v(0.37, 0.31) * mm});
            skLineSegment(sketch, "E459", {"start": v(0.37, 0.2) * mm, "end": v(0.36, 0.17) * mm});
            skLineSegment(sketch, "E460", {"start": v(0.36, 0.17) * mm, "end": v(0.36, 0.17) * mm});
            skLineSegment(sketch, "E461", {"start": v(0.36, 0.17) * mm, "end": v(0.36, 0.15) * mm});
            skLineSegment(sketch, "E462", {"start": v(0.26, 0) * mm, "end": v(0.22, -0.04) * mm});
            skLineSegment(sketch, "E463", {"start": v(0.22, -0.04) * mm, "end": v(0.2, -0.05) * mm});
            skLineSegment(sketch, "E464", {"start": v(0.2, -0.05) * mm, "end": v(0.2, -0.06) * mm});
            skLineSegment(sketch, "E465", {"start": v(0.1, -0.1) * mm, "end": v(0.04, -0.11) * mm});
            skLineSegment(sketch, "E466", {"start": v(0.04, -0.11) * mm, "end": v(0, -0.11) * mm});
            skLineSegment(sketch, "E467", {"start": v(0, -0.11) * mm, "end": v(-0.02, -0.11) * mm});
            skLineSegment(sketch, "E468", {"start": v(-0.02, -0.11) * mm, "end": v(-0.03, -0.11) * mm});
            skLineSegment(sketch, "E469", {"start": v(-0.03, -0.11) * mm, "end": v(-0.06, -0.1) * mm});
            skLineSegment(sketch, "E470", {"start": v(-0.15, -0.08) * mm, "end": v(-0.2, -0.06) * mm});
            skLineSegment(sketch, "E471", {"start": v(-0.2, -0.06) * mm, "end": v(-0.23, -0.03) * mm});
            skLineSegment(sketch, "E472", {"start": v(-0.23, -0.03) * mm, "end": v(-0.26, 0) * mm});
            skLineSegment(sketch, "E473", {"start": v(-0.26, 0) * mm, "end": v(-0.3, 0.03) * mm});
            skLineSegment(sketch, "E474", {"start": v(-0.3, 0.03) * mm, "end": v(-0.31, 0.06) * mm});
            skLineSegment(sketch, "E475", {"start": v(-0.31, 0.06) * mm, "end": v(-0.32, 0.07) * mm});
            skLineSegment(sketch, "E476", {"start": v(-0.32, 0.07) * mm, "end": v(-0.32, 0.08) * mm});
            skLineSegment(sketch, "E477", {"start": v(-0.32, 0.08) * mm, "end": v(-0.34, 0.1) * mm});
            skLineSegment(sketch, "E478", {"start": v(-0.34, 0.1) * mm, "end": v(-0.35, 0.15) * mm});
            skLineSegment(sketch, "E479", {"start": v(-0.36, 0.2) * mm, "end": v(-0.37, 0.23) * mm});
            skLineSegment(sketch, "E480", {"start": v(-0.37, 0.23) * mm, "end": v(-0.37, 0.24) * mm});
            skLineSegment(sketch, "E481", {"start": v(-0.37, 0.24) * mm, "end": v(-0.37, 0.25) * mm});
            skLineSegment(sketch, "E482", {"start": v(-0.37, 0.25) * mm, "end": v(-0.36, 0.3) * mm});
            skLineSegment(sketch, "E483", {"start": v(-0.35, 0.36) * mm, "end": v(-0.33, 0.41) * mm});
            skLineSegment(sketch, "E484", {"start": v(-0.33, 0.41) * mm, "end": v(-0.31, 0.45) * mm});
            skLineSegment(sketch, "E485", {"start": v(-0.31, 0.45) * mm, "end": v(-0.3, 0.46) * mm});
            skLineSegment(sketch, "E486", {"start": v(-0.3, 0.47) * mm, "end": v(-0.29, 0.49) * mm});
            skLineSegment(sketch, "E487", {"start": v(-0.29, 0.49) * mm, "end": v(-0.26, 0.51) * mm});
            skLineSegment(sketch, "E488", {"start": v(-0.23, 0.54) * mm, "end": v(-0.21, 0.56) * mm});
            skLineSegment(sketch, "E489", {"start": v(-0.21, 0.56) * mm, "end": v(-0.2, 0.56) * mm});
            skLineSegment(sketch, "E490", {"start": v(-0.2, 0.57) * mm, "end": v(-0.19, 0.57) * mm});
            skLineSegment(sketch, "E491", {"start": v(-0.19, 0.57) * mm, "end": v(-0.18, 0.58) * mm});
            skLineSegment(sketch, "E492", {"start": v(-0.18, 0.45) * mm, "end": v(-0.18, 0.45) * mm});
            skLineSegment(sketch, "E493", {"start": v(-0.18, 0.59) * mm, "end": v(-0.19, 0.6) * mm});
            skLineSegment(sketch, "E494", {"start": v(-0.19, 0.6) * mm, "end": v(-0.2, 0.61) * mm});
            skLineSegment(sketch, "E495", {"start": v(-0.2, 0.63) * mm, "end": v(-0.21, 0.64) * mm});
            skLineSegment(sketch, "E496", {"start": v(-0.21, 0.64) * mm, "end": v(-0.22, 0.66) * mm});
            skLineSegment(sketch, "E497", {"start": v(-0.28, 0.77) * mm, "end": v(-0.29, 0.78) * mm});
            skLineSegment(sketch, "E498", {"start": v(-0.29, 0.78) * mm, "end": v(-0.3, 0.78) * mm});
            skLineSegment(sketch, "E499", {"start": v(-0.3, 0.78) * mm, "end": v(-0.3, 0.78) * mm});
            skLineSegment(sketch, "E500", {"start": v(-0.3, 0.78) * mm, "end": v(-0.3, 0.77) * mm});
            skLineSegment(sketch, "E501", {"start": v(-0.3, 0.77) * mm, "end": v(-0.31, 0.77) * mm});
            skLineSegment(sketch, "E502", {"start": v(-0.31, 0.77) * mm, "end": v(-0.32, 0.76) * mm});
            skLineSegment(sketch, "E503", {"start": v(-0.32, 0.76) * mm, "end": v(-0.32, 0.76) * mm});
            skLineSegment(sketch, "E504", {"start": v(-0.3, 0.77) * mm, "end": v(-0.3, 0.78) * mm});
            skLineSegment(sketch, "E505", {"start": v(-0.31, 0.77) * mm, "end": v(-0.3, 0.77) * mm});
            skLineSegment(sketch, "E506", {"start": v(-0.32, 0.77) * mm, "end": v(-0.34, 0.75) * mm});
            skLineSegment(sketch, "E507", {"start": v(-0.34, 0.75) * mm, "end": v(-0.38, 0.72) * mm});
            skLineSegment(sketch, "E508", {"start": v(-0.38, 0.72) * mm, "end": v(-0.44, 0.66) * mm});
            skLineSegment(sketch, "E509", {"start": v(-0.44, 0.66) * mm, "end": v(-0.49, 0.6) * mm});
            skLineSegment(sketch, "E510", {"start": v(-0.49, 0.6) * mm, "end": v(-0.53, 0.54) * mm});
            skLineSegment(sketch, "E511", {"start": v(-0.53, 0.54) * mm, "end": v(-0.56, 0.47) * mm});
            skLineSegment(sketch, "E512", {"start": v(-0.56, 0.47) * mm, "end": v(-0.58, 0.4) * mm});
            skLineSegment(sketch, "E513", {"start": v(-0.58, 0.4) * mm, "end": v(-0.6, 0.31) * mm});
            skLineSegment(sketch, "E514", {"start": v(-0.6, 0.31) * mm, "end": v(-0.6, 0.26) * mm});
            skLineSegment(sketch, "E515", {"start": v(-0.6, 0.26) * mm, "end": v(-0.6, 0.24) * mm});
            skLineSegment(sketch, "E516", {"start": v(-0.6, 0.24) * mm, "end": v(-0.6, 0.22) * mm});
            skLineSegment(sketch, "E517", {"start": v(-0.6, 0.22) * mm, "end": v(-0.59, 0.16) * mm});
            skLineSegment(sketch, "E518", {"start": v(-0.59, 0.16) * mm, "end": v(-0.57, 0.1) * mm});
            skLineSegment(sketch, "E519", {"start": v(-0.57, 0.1) * mm, "end": v(-0.55, 0.03) * mm});
            skLineSegment(sketch, "E520", {"start": v(-0.55, 0.03) * mm, "end": v(-0.52, -0.03) * mm});
            skLineSegment(sketch, "E521", {"start": v(-0.52, -0.03) * mm, "end": v(-0.48, -0.09) * mm});
            skLineSegment(sketch, "E522", {"start": v(-0.48, -0.09) * mm, "end": v(-0.44, -0.14) * mm});
            skLineSegment(sketch, "E523", {"start": v(-0.44, -0.14) * mm, "end": v(-0.4, -0.19) * mm});
            skLineSegment(sketch, "E524", {"start": v(-0.4, -0.19) * mm, "end": v(-0.34, -0.23) * mm});
            skLineSegment(sketch, "E525", {"start": v(-0.34, -0.23) * mm, "end": v(-0.28, -0.26) * mm});
            skLineSegment(sketch, "E526", {"start": v(-0.28, -0.26) * mm, "end": v(-0.22, -0.3) * mm});
            skLineSegment(sketch, "E527", {"start": v(-0.22, -0.3) * mm, "end": v(-0.16, -0.31) * mm});
            skLineSegment(sketch, "E528", {"start": v(-0.16, -0.31) * mm, "end": v(-0.1, -0.33) * mm});
            skLineSegment(sketch, "E529", {"start": v(-0.1, -0.33) * mm, "end": v(-0.02, -0.34) * mm});
            skLineSegment(sketch, "E530", {"start": v(-0.02, -0.34) * mm, "end": v(0.04, -0.34) * mm});
            skLineSegment(sketch, "E531", {"start": v(0.11, -0.33) * mm, "end": v(0.17, -0.31) * mm});
            skLineSegment(sketch, "E532", {"start": v(0.17, -0.31) * mm, "end": v(0.18, -0.3) * mm});
            skLineSegment(sketch, "E533", {"start": v(0.18, -0.3) * mm, "end": v(0.2, -0.3) * mm});
            skLineSegment(sketch, "E534", {"start": v(0.2, -0.3) * mm, "end": v(0.23, -0.3) * mm});
            skLineSegment(sketch, "E535", {"start": v(0.23, -0.3) * mm, "end": v(0.27, -0.27) * mm});
            skLineSegment(sketch, "E536", {"start": v(0.27, -0.27) * mm, "end": v(0.31, -0.25) * mm});
            skLineSegment(sketch, "E537", {"start": v(0.31, -0.25) * mm, "end": v(0.35, -0.23) * mm});
            skLineSegment(sketch, "E538", {"start": v(0.38, -0.2) * mm, "end": v(0.42, -0.17) * mm});
            skLineSegment(sketch, "E539", {"start": v(0.42, -0.17) * mm, "end": v(0.45, -0.14) * mm});
            skLineSegment(sketch, "E540", {"start": v(0.53, -0.03) * mm, "end": v(0.55, 0.01) * mm});
            skLineSegment(sketch, "E541", {"start": v(0.55, 0.01) * mm, "end": v(0.56, 0.06) * mm});
            skLineSegment(sketch, "E542", {"start": v(0.56, 0.06) * mm, "end": v(0.58, 0.1) * mm});
            skLineSegment(sketch, "E543", {"start": v(0.59, 0.14) * mm, "end": v(0.6, 0.19) * mm});
            skLineSegment(sketch, "E544", {"start": v(0.6, 0.19) * mm, "end": v(0.6, 0.22) * mm});
            skLineSegment(sketch, "E545", {"start": v(0.6, 0.22) * mm, "end": v(0.6, 0.24) * mm});
            skLineSegment(sketch, "E546", {"start": v(0.6, 0.24) * mm, "end": v(0.6, 0.26) * mm});
            skLineSegment(sketch, "E547", {"start": v(0.6, 0.26) * mm, "end": v(0.6, 0.31) * mm});
            skLineSegment(sketch, "E548", {"start": v(0.6, 0.31) * mm, "end": v(0.59, 0.4) * mm});
            skLineSegment(sketch, "E549", {"start": v(0.59, 0.4) * mm, "end": v(0.57, 0.46) * mm});
            skLineSegment(sketch, "E550", {"start": v(0.5, 0.6) * mm, "end": v(0.45, 0.66) * mm});
            skLineSegment(sketch, "E551", {"start": v(0.45, 0.66) * mm, "end": v(0.4, 0.71) * mm});
            skLineSegment(sketch, "E552", {"start": v(0.4, 0.71) * mm, "end": v(0.35, 0.75) * mm});
            skLineSegment(sketch, "E553", {"start": v(0.33, 0.76) * mm, "end": v(0.32, 0.77) * mm});
            skLineSegment(sketch, "E554", {"start": v(0.32, 0.77) * mm, "end": v(0.31, 0.77) * mm});
            skLineSegment(sketch, "E555", {"start": v(0.31, 0.77) * mm, "end": v(0.3, 0.78) * mm});
            skLineSegment(sketch, "E556", {"start": v(0.3, 0.78) * mm, "end": v(0.3, 0.78) * mm});
            skLineSegment(sketch, "E557", {"start": v(0.3, 0.78) * mm, "end": v(0.3, 0.77) * mm});
            skLineSegment(sketch, "E558", {"start": v(0.3, 0.77) * mm, "end": v(0.29, 0.76) * mm});
            skLineSegment(sketch, "E559", {"start": v(0.29, 0.76) * mm, "end": v(0.28, 0.75) * mm});
            skLineSegment(sketch, "E560", {"start": v(0.28, 0.75) * mm, "end": v(0.28, 0.74) * mm});
            skLineSegment(sketch, "E561", {"start": v(0.28, 0.74) * mm, "end": v(0.27, 0.73) * mm});
            skLineSegment(sketch, "E562", {"start": v(0.27, 0.73) * mm, "end": v(0.26, 0.7) * mm});
            skLineSegment(sketch, "E563", {"start": v(0.23, 0.65) * mm, "end": v(0.23, 0.65) * mm});
            skLineSegment(sketch, "E564", {"start": v(0.23, 0.65) * mm, "end": v(0.19, 0.58) * mm});
            skLineSegment(sketch, "E565", {"start": v(0.19, 0.58) * mm, "end": v(0.22, 0.56) * mm});
            skLineSegment(sketch, "E566", {"start": v(0.22, 0.56) * mm, "end": v(0.22, 0.56) * mm});
            skLineSegment(sketch, "E567", {"start": v(0.22, 0.56) * mm, "end": v(0.24, 0.54) * mm});
            skLineSegment(sketch, "E568", {"start": v(0.24, 0.54) * mm, "end": v(0.27, 0.52) * mm});
            skLineSegment(sketch, "E569", {"start": v(0.27, 0.52) * mm, "end": v(0.3, 0.5) * mm});
            skLineSegment(sketch, "E570", {"start": v(0.3, 0.5) * mm, "end": v(0.3, 0.47) * mm});
            skLineSegment(sketch, "E571", {"start": v(0.3, 0.47) * mm, "end": v(0.3, 0.47) * mm});
            skLineSegment(sketch, "E572", {"start": v(0.3, 0.47) * mm, "end": v(0.32, 0.46) * mm});
            skLineSegment(sketch, "E573", {"start": v(0.32, 0.46) * mm, "end": v(0.33, 0.43) * mm});
            skLineSegment(sketch, "E574", {"start": v(0.35, 0.4) * mm, "end": v(0.36, 0.36) * mm});
            skLineSegment(sketch, "E575", {"start": v(0.36, 0.36) * mm, "end": v(0.37, 0.33) * mm});
            skLineSegment(sketch, "E576", {"start": v(0.37, 0.33) * mm, "end": v(0.37, 0.32) * mm});
            skLineSegment(sketch, "E577", {"start": v(0.37, 0.31) * mm, "end": v(0.37, 0.28) * mm});
            skLineSegment(sketch, "E578", {"start": v(0.37, 0.2) * mm, "end": v(0.36, 0.18) * mm});
            skLineSegment(sketch, "E579", {"start": v(0.36, 0.18) * mm, "end": v(0.36, 0.17) * mm});
            skLineSegment(sketch, "E580", {"start": v(0.34, 0.1) * mm, "end": v(0.3, 0.05) * mm});
            skLineSegment(sketch, "E581", {"start": v(0.3, 0.05) * mm, "end": v(0.26, 0) * mm});
            skLineSegment(sketch, "E582", {"start": v(0.22, -0.04) * mm, "end": v(0.21, -0.04) * mm});
            skLineSegment(sketch, "E583", {"start": v(0.21, -0.04) * mm, "end": v(0.2, -0.05) * mm});
            skLineSegment(sketch, "E584", {"start": v(0.2, -0.05) * mm, "end": v(0.16, -0.07) * mm});
            skLineSegment(sketch, "E585", {"start": v(0.16, -0.07) * mm, "end": v(0.1, -0.1) * mm});
            skLineSegment(sketch, "E586", {"start": v(0.1, -0.1) * mm, "end": v(0.05, -0.1) * mm});
            skLineSegment(sketch, "E587", {"start": v(0.05, -0.1) * mm, "end": v(0, -0.1) * mm});
            skLineSegment(sketch, "E588", {"start": v(0, -0.1) * mm, "end": v(-0.01, -0.1) * mm});
            skLineSegment(sketch, "E589", {"start": v(-0.01, -0.1) * mm, "end": v(-0.03, -0.1) * mm});
            skLineSegment(sketch, "E590", {"start": v(-0.03, -0.1) * mm, "end": v(-0.06, -0.1) * mm});
            skLineSegment(sketch, "E591", {"start": v(-0.15, -0.08) * mm, "end": v(-0.19, -0.05) * mm});
            skLineSegment(sketch, "E592", {"start": v(-0.19, -0.05) * mm, "end": v(-0.23, -0.03) * mm});
            skLineSegment(sketch, "E593", {"start": v(-0.26, 0) * mm, "end": v(-0.29, 0.04) * mm});
            skLineSegment(sketch, "E594", {"start": v(-0.29, 0.04) * mm, "end": v(-0.3, 0.07) * mm});
            skLineSegment(sketch, "E595", {"start": v(-0.3, 0.07) * mm, "end": v(-0.32, 0.08) * mm});
            skLineSegment(sketch, "E596", {"start": v(-0.32, 0.08) * mm, "end": v(-0.32, 0.09) * mm});
            skLineSegment(sketch, "E597", {"start": v(-0.32, 0.09) * mm, "end": v(-0.34, 0.11) * mm});
            skLineSegment(sketch, "E598", {"start": v(-0.34, 0.11) * mm, "end": v(-0.35, 0.15) * mm});
            skLineSegment(sketch, "E599", {"start": v(-0.36, 0.24) * mm, "end": v(-0.36, 0.26) * mm});
            skLineSegment(sketch, "E600", {"start": v(-0.36, 0.26) * mm, "end": v(-0.36, 0.3) * mm});
            skLineSegment(sketch, "E601", {"start": v(-0.35, 0.36) * mm, "end": v(-0.33, 0.42) * mm});
            skLineSegment(sketch, "E602", {"start": v(-0.33, 0.42) * mm, "end": v(-0.31, 0.46) * mm});
            skLineSegment(sketch, "E603", {"start": v(-0.31, 0.46) * mm, "end": v(-0.3, 0.47) * mm});
            skLineSegment(sketch, "E604", {"start": v(-0.3, 0.47) * mm, "end": v(-0.3, 0.47) * mm});
            skLineSegment(sketch, "E605", {"start": v(-0.3, 0.47) * mm, "end": v(-0.28, 0.5) * mm});
            skLineSegment(sketch, "E606", {"start": v(-0.28, 0.5) * mm, "end": v(-0.26, 0.52) * mm});
            skLineSegment(sketch, "E607", {"start": v(-0.26, 0.52) * mm, "end": v(-0.23, 0.55) * mm});
            skLineSegment(sketch, "E608", {"start": v(-0.23, 0.55) * mm, "end": v(-0.21, 0.56) * mm});
            skLineSegment(sketch, "E609", {"start": v(-0.21, 0.56) * mm, "end": v(-0.2, 0.57) * mm});
            skLineSegment(sketch, "E610", {"start": v(-0.2, 0.57) * mm, "end": v(-0.2, 0.57) * mm});
            skLineSegment(sketch, "E611", {"start": v(-0.2, 0.57) * mm, "end": v(-0.19, 0.58) * mm});
            skLineSegment(sketch, "E612", {"start": v(-0.19, 0.58) * mm, "end": v(-0.18, 0.58) * mm});
            skLineSegment(sketch, "E613", {"start": v(-0.18, 0.59) * mm, "end": v(-0.18, 0.59) * mm});
            skLineSegment(sketch, "E614", {"start": v(-0.18, 0.6) * mm, "end": v(-0.19, 0.6) * mm});
            skLineSegment(sketch, "E615", {"start": v(-0.19, 0.6) * mm, "end": v(-0.2, 0.62) * mm});
            skLineSegment(sketch, "E616", {"start": v(-0.2, 0.62) * mm, "end": v(-0.2, 0.63) * mm});
            skLineSegment(sketch, "E617", {"start": v(-0.2, 0.63) * mm, "end": v(-0.21, 0.65) * mm});
            skLineSegment(sketch, "E618", {"start": v(-0.21, 0.65) * mm, "end": v(-0.22, 0.67) * mm});
            skLineSegment(sketch, "E619", {"start": v(-0.22, 0.67) * mm, "end": v(-0.23, 0.69) * mm});
            skLineSegment(sketch, "E620", {"start": v(-0.23, 0.69) * mm, "end": v(-0.24, 0.7) * mm});
            skLineSegment(sketch, "E621", {"start": v(-0.25, 0.72) * mm, "end": v(-0.26, 0.74) * mm});
            skLineSegment(sketch, "E622", {"start": v(-0.26, 0.74) * mm, "end": v(-0.27, 0.75) * mm});
            skLineSegment(sketch, "E623", {"start": v(-0.27, 0.75) * mm, "end": v(-0.28, 0.77) * mm});
            skLineSegment(sketch, "E624", {"start": v(-0.3, 0.77) * mm, "end": v(-0.32, 0.77) * mm});
            skLineSegment(sketch, "E625", {"start": v(-0.32, 0.77) * mm, "end": v(-0.32, 0.77) * mm});
            skLineSegment(sketch, "E626", {"start": v(-0.34, 0.75) * mm, "end": v(-0.39, 0.72) * mm});
            skLineSegment(sketch, "E627", {"start": v(-0.39, 0.72) * mm, "end": v(-0.44, 0.66) * mm});
            skLineSegment(sketch, "E628", {"start": v(-0.5, 0.6) * mm, "end": v(-0.53, 0.54) * mm});
            skLineSegment(sketch, "E629", {"start": v(-0.58, 0.4) * mm, "end": v(-0.6, 0.32) * mm});
            skLineSegment(sketch, "E630", {"start": v(-0.6, 0.32) * mm, "end": v(-0.6, 0.26) * mm});
            skLineSegment(sketch, "E631", {"start": v(-0.34, -0.23) * mm, "end": v(-0.29, -0.26) * mm});
            skLineSegment(sketch, "E632", {"start": v(-0.29, -0.26) * mm, "end": v(-0.23, -0.3) * mm});
            skLineSegment(sketch, "E633", {"start": v(-0.23, -0.3) * mm, "end": v(-0.16, -0.31) * mm});
            skLineSegment(sketch, "E634", {"start": v(-0.1, -0.33) * mm, "end": v(-0.03, -0.34) * mm});
            skLineSegment(sketch, "E635", {"start": v(0.11, -0.33) * mm, "end": v(0.16, -0.31) * mm});
            skLineSegment(sketch, "E636", {"start": v(0.16, -0.31) * mm, "end": v(0.18, -0.3) * mm});
            skLineSegment(sketch, "E637", {"start": v(0.2, -0.3) * mm, "end": v(0.22, -0.3) * mm});
            skLineSegment(sketch, "E638", {"start": v(0.22, -0.3) * mm, "end": v(0.27, -0.27) * mm});
            skLineSegment(sketch, "E639", {"start": v(0.27, -0.27) * mm, "end": v(0.3, -0.25) * mm});
            skLineSegment(sketch, "E640", {"start": v(0.3, -0.25) * mm, "end": v(0.34, -0.23) * mm});
            skLineSegment(sketch, "E641", {"start": v(0.34, -0.23) * mm, "end": v(0.38, -0.2) * mm});
            skLineSegment(sketch, "E642", {"start": v(0.38, -0.2) * mm, "end": v(0.41, -0.17) * mm});
            skLineSegment(sketch, "E643", {"start": v(0.41, -0.17) * mm, "end": v(0.45, -0.14) * mm});
            skLineSegment(sketch, "E644", {"start": v(0.45, -0.14) * mm, "end": v(0.47, -0.1) * mm});
            skLineSegment(sketch, "E645", {"start": v(0.47, -0.1) * mm, "end": v(0.5, -0.06) * mm});
            skLineSegment(sketch, "E646", {"start": v(0.5, -0.06) * mm, "end": v(0.52, -0.03) * mm});
            skLineSegment(sketch, "E647", {"start": v(0.52, -0.03) * mm, "end": v(0.54, 0.01) * mm});
            skLineSegment(sketch, "E648", {"start": v(0.54, 0.01) * mm, "end": v(0.56, 0.06) * mm});
            skLineSegment(sketch, "E649", {"start": v(0.56, 0.06) * mm, "end": v(0.57, 0.1) * mm});
            skLineSegment(sketch, "E650", {"start": v(0.57, 0.1) * mm, "end": v(0.59, 0.14) * mm});
            skLineSegment(sketch, "E651", {"start": v(0.6, 0.31) * mm, "end": v(0.58, 0.4) * mm});
            skLineSegment(sketch, "E652", {"start": v(0.58, 0.4) * mm, "end": v(0.56, 0.46) * mm});
            skLineSegment(sketch, "E653", {"start": v(0.4, 0.71) * mm, "end": v(0.34, 0.75) * mm});
            skLineSegment(sketch, "E654", {"start": v(0.34, 0.75) * mm, "end": v(0.33, 0.76) * mm});
            skLineSegment(sketch, "E655", {"start": v(0.3, 0.77) * mm, "end": v(0.28, 0.76) * mm});
            skLineSegment(sketch, "E656", {"start": v(0.28, 0.76) * mm, "end": v(0.28, 0.75) * mm});
            skLineSegment(sketch, "E657", {"start": v(0.28, 0.74) * mm, "end": v(0.27, 0.74) * mm});
            skLineSegment(sketch, "E658", {"start": v(0.27, 0.74) * mm, "end": v(0.27, 0.73) * mm});
            skLineSegment(sketch, "E659", {"start": v(0.27, 0.73) * mm, "end": v(0.25, 0.7) * mm});
            skLineSegment(sketch, "E660", {"start": v(0.24, 0.67) * mm, "end": v(0.22, 0.65) * mm});
            skLineSegment(sketch, "E661", {"start": v(0.22, 0.65) * mm, "end": v(0.22, 0.65) * mm});
            skLineSegment(sketch, "E662", {"start": v(0.21, 0.57) * mm, "end": v(0.22, 0.56) * mm});
            skLineSegment(sketch, "E663", {"start": v(0.22, 0.56) * mm, "end": v(0.24, 0.55) * mm});
            skLineSegment(sketch, "E664", {"start": v(0.24, 0.55) * mm, "end": v(0.26, 0.52) * mm});
            skLineSegment(sketch, "E665", {"start": v(0.26, 0.52) * mm, "end": v(0.29, 0.5) * mm});
            skLineSegment(sketch, "E666", {"start": v(0.29, 0.5) * mm, "end": v(0.3, 0.48) * mm});
            skLineSegment(sketch, "E667", {"start": v(0.3, 0.48) * mm, "end": v(0.3, 0.47) * mm});
            skLineSegment(sketch, "E668", {"start": v(0.31, 0.46) * mm, "end": v(0.33, 0.43) * mm});
            skLineSegment(sketch, "E669", {"start": v(0.33, 0.43) * mm, "end": v(0.34, 0.4) * mm});
            skLineSegment(sketch, "E670", {"start": v(0.34, 0.4) * mm, "end": v(0.36, 0.36) * mm});
            skLineSegment(sketch, "E671", {"start": v(0.36, 0.36) * mm, "end": v(0.36, 0.33) * mm});
            skLineSegment(sketch, "E672", {"start": v(0.36, 0.33) * mm, "end": v(0.36, 0.32) * mm});
            skLineSegment(sketch, "E673", {"start": v(0.37, 0.31) * mm, "end": v(0.37, 0.29) * mm});
            skLineSegment(sketch, "E674", {"start": v(0.37, 0.29) * mm, "end": v(0.37, 0.24) * mm});
            skLineSegment(sketch, "E675", {"start": v(0.37, 0.24) * mm, "end": v(0.36, 0.2) * mm});
            skLineSegment(sketch, "E676", {"start": v(0.36, 0.2) * mm, "end": v(0.36, 0.18) * mm});
            skLineSegment(sketch, "E677", {"start": v(0.36, 0.17) * mm, "end": v(0.35, 0.16) * mm});
            skLineSegment(sketch, "E678", {"start": v(0.35, 0.16) * mm, "end": v(0.33, 0.1) * mm});
            skLineSegment(sketch, "E679", {"start": v(0.33, 0.1) * mm, "end": v(0.3, 0.05) * mm});
            skLineSegment(sketch, "E680", {"start": v(0.26, 0) * mm, "end": v(0.22, -0.03) * mm});
            skLineSegment(sketch, "E681", {"start": v(0.22, -0.03) * mm, "end": v(0.2, -0.04) * mm});
            skLineSegment(sketch, "E682", {"start": v(0.2, -0.04) * mm, "end": v(0.2, -0.05) * mm});
            skLineSegment(sketch, "E683", {"start": v(0.2, -0.05) * mm, "end": v(0.15, -0.07) * mm});
            skLineSegment(sketch, "E684", {"start": v(0.15, -0.07) * mm, "end": v(0.1, -0.1) * mm});
            skLineSegment(sketch, "E685", {"start": v(0.1, -0.1) * mm, "end": v(0.04, -0.1) * mm});
            skLineSegment(sketch, "E686", {"start": v(0.04, -0.1) * mm, "end": v(0, -0.1) * mm});
            skLineSegment(sketch, "E687", {"start": v(0, -0.1) * mm, "end": v(-0.02, -0.1) * mm});
            skLineSegment(sketch, "E688", {"start": v(-0.02, -0.1) * mm, "end": v(-0.03, -0.1) * mm});
            skLineSegment(sketch, "E689", {"start": v(-0.03, -0.1) * mm, "end": v(-0.07, -0.1) * mm});
            skLineSegment(sketch, "E690", {"start": v(-0.07, -0.1) * mm, "end": v(-0.11, -0.1) * mm});
            skLineSegment(sketch, "E691", {"start": v(-0.11, -0.1) * mm, "end": v(-0.15, -0.07) * mm});
            skLineSegment(sketch, "E692", {"start": v(-0.15, -0.07) * mm, "end": v(-0.2, -0.05) * mm});
            skLineSegment(sketch, "E693", {"start": v(-0.2, -0.05) * mm, "end": v(-0.23, -0.03) * mm});
            skLineSegment(sketch, "E694", {"start": v(-0.26, 0) * mm, "end": v(-0.3, 0.04) * mm});
            skLineSegment(sketch, "E695", {"start": v(-0.3, 0.04) * mm, "end": v(-0.31, 0.07) * mm});
            skLineSegment(sketch, "E696", {"start": v(-0.32, 0.08) * mm, "end": v(-0.33, 0.09) * mm});
            skLineSegment(sketch, "E697", {"start": v(-0.33, 0.09) * mm, "end": v(-0.34, 0.12) * mm});
            skLineSegment(sketch, "E698", {"start": v(-0.34, 0.12) * mm, "end": v(-0.35, 0.16) * mm});
            skLineSegment(sketch, "E699", {"start": v(-0.35, 0.16) * mm, "end": v(-0.36, 0.2) * mm});
            skLineSegment(sketch, "E700", {"start": v(-0.37, 0.24) * mm, "end": v(-0.37, 0.26) * mm});
            skLineSegment(sketch, "E701", {"start": v(-0.37, 0.26) * mm, "end": v(-0.37, 0.3) * mm});
            skLineSegment(sketch, "E702", {"start": v(-0.37, 0.3) * mm, "end": v(-0.36, 0.36) * mm});
            skLineSegment(sketch, "E703", {"start": v(-0.36, 0.36) * mm, "end": v(-0.34, 0.42) * mm});
            skLineSegment(sketch, "E704", {"start": v(-0.34, 0.42) * mm, "end": v(-0.31, 0.46) * mm});
            skLineSegment(sketch, "E705", {"start": v(-0.3, 0.47) * mm, "end": v(-0.3, 0.48) * mm});
            skLineSegment(sketch, "E706", {"start": v(-0.3, 0.48) * mm, "end": v(-0.29, 0.5) * mm});
            skLineSegment(sketch, "E707", {"start": v(-0.29, 0.5) * mm, "end": v(-0.26, 0.52) * mm});
            skLineSegment(sketch, "E708", {"start": v(-0.23, 0.55) * mm, "end": v(-0.22, 0.56) * mm});
            skLineSegment(sketch, "E709", {"start": v(-0.22, 0.56) * mm, "end": v(-0.2, 0.57) * mm});
            skLineSegment(sketch, "E710", {"start": v(-0.2, 0.57) * mm, "end": v(-0.2, 0.58) * mm});
            skLineSegment(sketch, "E711", {"start": v(-0.2, 0.58) * mm, "end": v(-0.18, 0.58) * mm});
            skLineSegment(sketch, "E712", {"start": v(-0.18, 0.4) * mm, "end": v(-0.18, 0.4) * mm});
            skLineSegment(sketch, "E713", {"start": v(-0.19, 0.6) * mm, "end": v(-0.2, 0.6) * mm});
            skLineSegment(sketch, "E714", {"start": v(-0.2, 0.6) * mm, "end": v(-0.2, 0.62) * mm});
            skLineSegment(sketch, "E715", {"start": v(-0.2, 0.63) * mm, "end": v(-0.22, 0.65) * mm});
            skLineSegment(sketch, "E716", {"start": v(-0.22, 0.65) * mm, "end": v(-0.23, 0.67) * mm});
            skLineSegment(sketch, "E717", {"start": v(-0.23, 0.67) * mm, "end": v(-0.24, 0.69) * mm});
            skLineSegment(sketch, "E718", {"start": v(-0.24, 0.69) * mm, "end": v(-0.25, 0.7) * mm});
            skLineSegment(sketch, "E719", {"start": v(-0.25, 0.7) * mm, "end": v(-0.26, 0.72) * mm});
            skLineSegment(sketch, "E720", {"start": v(-0.26, 0.72) * mm, "end": v(-0.27, 0.74) * mm});
            skLineSegment(sketch, "E721", {"start": v(-0.27, 0.74) * mm, "end": v(-0.27, 0.75) * mm});
            skLineSegment(sketch, "E722", {"start": v(-0.3, 0.78) * mm, "end": v(-0.3, 0.79) * mm});
            skLineSegment(sketch, "E723", {"start": v(-0.3, 0.79) * mm, "end": v(-0.3, 0.79) * mm});
            skLineSegment(sketch, "E724", {"start": v(-0.3, 0.79) * mm, "end": v(-0.3, 0.78) * mm});
            skLineSegment(sketch, "E725", {"start": v(-0.3, 0.78) * mm, "end": v(-0.31, 0.77) * mm});
            skLineSegment(sketch, "E726", {"start": v(-0.31, 0.77) * mm, "end": v(-0.32, 0.77) * mm});
            skLineSegment(sketch, "E727", {"start": v(-0.31, 0.77) * mm, "end": v(-0.3, 0.78) * mm});
            skSolve(sketch);
        }
        {
            var Q0;
            Q0=makeQuery(id+"F6.imprint","IMPRINT",FACE,{"disambiguationData":[TD([[makeQuery(id+"F6.imprint","IMPRINT",EDGE,{"derivedFrom":sQuery(id+"F6.wireOp",EDGE,"E244")}),1.0]])]});
            var Q1;
            Q1=makeQuery(id+"F6.imprint","IMPRINT",FACE,{"disambiguationData":[TD([[makeQuery(id+"F6.imprint","IMPRINT",EDGE,{"derivedFrom":sQuery(id+"F6.wireOp",EDGE,"E182")}),1.0]])]});
            extrude(context, id + "F7", {"entities" : qUnion([Q0, Q1]), "depth" : 0.13 * mm, "offsetDistance" : 25.4 * mm});
        }
    });
